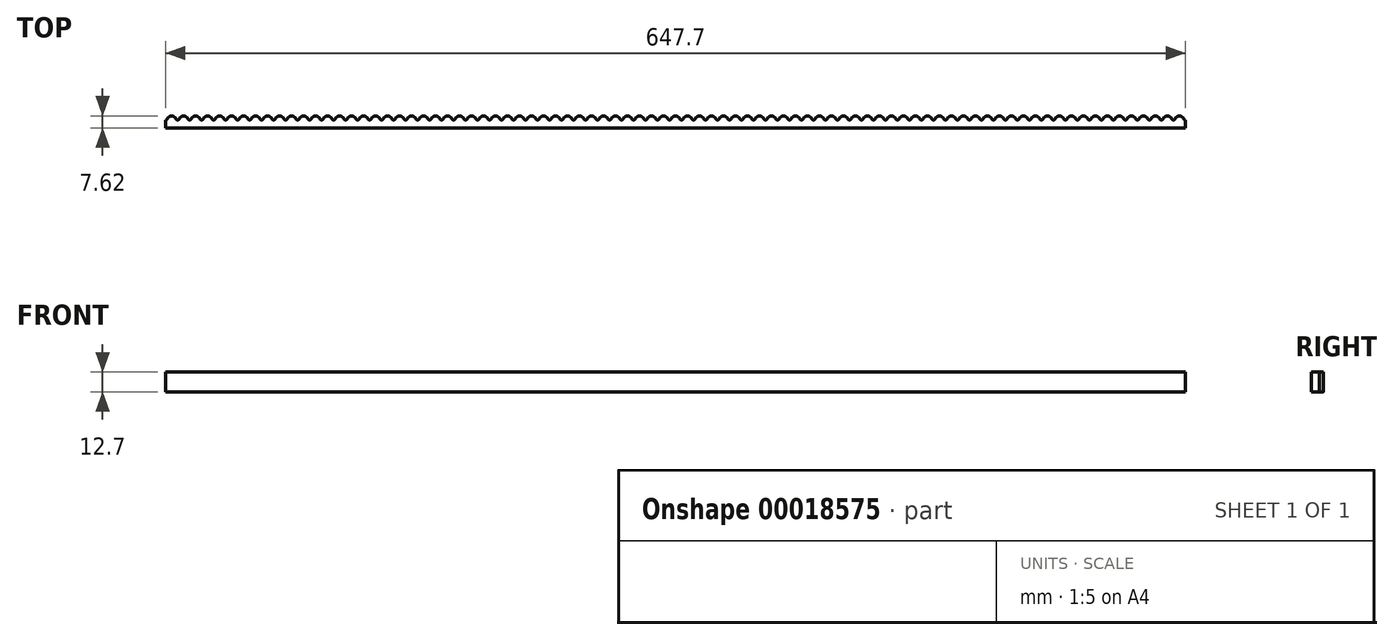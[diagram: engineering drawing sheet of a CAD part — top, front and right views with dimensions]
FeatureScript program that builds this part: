
annotation { "Feature Type Name" : "Feature", "Feature Type Description" : "" }
export const myFeature = defineFeature(function(context is Context, id is Id, definition is map)
    precondition{}
    {
        {
            var Q0;
            Q0=qCreatedBy(makeId("Top.planeOp"),FACE);
            var sketch = newSketch(context, id + "F0", { "sketchPlane" : qUnion([Q0])});
            skLineSegment(sketch, "E0.bottom", {"start": v(0, 0) * mm, "end": v(7.62, 0) * mm});
            skLineSegment(sketch, "E0.top", {"start": v(0, 7.62) * mm, "end": v(7.62, 7.62) * mm, "construction": true});
            skLineSegment(sketch, "E0.left", {"start": v(0, 0) * mm, "end": v(0, 7.62) * mm, "construction": true});
            skLineSegment(sketch, "E0.right", {"start": v(7.62, 0) * mm, "end": v(7.62, 7.62) * mm, "construction": true});
            skLineSegment(sketch, "E1", {"start": v(0, 5.08) * mm, "end": v(7.62, 5.08) * mm, "construction": true});
            skArc(sketch, "E2", {"start": v(0, 5.08) * mm, "mid": v(0.55, 5.21) * mm, "end": v(0.98, 5.58) * mm});
            skArc(sketch, "E3", {"start": v(5.98, 6.5) * mm, "mid": v(3.81, 7.62) * mm, "end": v(1.64, 6.5) * mm});
            skArc(sketch, "E4", {"start": v(6.64, 5.58) * mm, "mid": v(7.07, 5.21) * mm, "end": v(7.62, 5.08) * mm});
            skLineSegment(sketch, "E5", {"start": v(3.8, 5.08) * mm, "end": v(3.8, 7.62) * mm, "construction": true});
            skLineSegment(sketch, "E6", {"start": v(0.98, 5.58) * mm, "end": v(1.64, 6.5) * mm});
            skLineSegment(sketch, "E7", {"start": v(5.98, 6.5) * mm, "end": v(6.64, 5.58) * mm});
            skPoint(sketch, "E8.orphan", {"position": v(1.2, 6.28) * mm});
            skPoint(sketch, "E9.orphan", {"position": v(1.5, 6.28) * mm});
            skPoint(sketch, "E10.orphan", {"position": v(6.12, 6.28) * mm});
            skPoint(sketch, "E11.orphan", {"position": v(6.42, 6.28) * mm});
            skLineSegment(sketch, "E12.1.0.0", {"start": v(7.62, 0) * mm, "end": v(15.24, 0) * mm});
            skArc(sketch, "E12.1.0.1", {"start": v(13.6, 6.5) * mm, "mid": v(11.43, 7.62) * mm, "end": v(9.26, 6.5) * mm});
            skLineSegment(sketch, "E12.1.0.2", {"start": v(13.6, 6.5) * mm, "end": v(14.26, 5.58) * mm});
            skArc(sketch, "E12.1.0.3", {"start": v(7.62, 5.08) * mm, "mid": v(8.17, 5.21) * mm, "end": v(8.6, 5.58) * mm});
            skPoint(sketch, "E12.1.0.4", {"position": v(14.04, 6.28) * mm});
            skLineSegment(sketch, "E12.1.0.5", {"start": v(8.6, 5.58) * mm, "end": v(9.26, 6.5) * mm});
            skArc(sketch, "E12.1.0.6", {"start": v(14.26, 5.58) * mm, "mid": v(14.7, 5.21) * mm, "end": v(15.24, 5.08) * mm});
            skPoint(sketch, "E12.1.0.7", {"position": v(8.82, 6.28) * mm});
            skLineSegment(sketch, "E12.2.0.0", {"start": v(15.24, 0) * mm, "end": v(22.86, 0) * mm});
            skArc(sketch, "E12.2.0.1", {"start": v(21.22, 6.5) * mm, "mid": v(19.05, 7.62) * mm, "end": v(16.88, 6.5) * mm});
            skLineSegment(sketch, "E12.2.0.2", {"start": v(21.22, 6.5) * mm, "end": v(21.88, 5.58) * mm});
            skArc(sketch, "E12.2.0.3", {"start": v(15.24, 5.08) * mm, "mid": v(15.79, 5.21) * mm, "end": v(16.22, 5.58) * mm});
            skPoint(sketch, "E12.2.0.4", {"position": v(21.66, 6.28) * mm});
            skLineSegment(sketch, "E12.2.0.5", {"start": v(16.22, 5.58) * mm, "end": v(16.88, 6.5) * mm});
            skArc(sketch, "E12.2.0.6", {"start": v(21.88, 5.58) * mm, "mid": v(22.31, 5.21) * mm, "end": v(22.86, 5.08) * mm});
            skPoint(sketch, "E12.2.0.7", {"position": v(16.44, 6.28) * mm});
            skLineSegment(sketch, "E12.3.0.0", {"start": v(22.86, 0) * mm, "end": v(30.48, 0) * mm});
            skArc(sketch, "E12.3.0.1", {"start": v(28.84, 6.5) * mm, "mid": v(26.67, 7.62) * mm, "end": v(24.5, 6.5) * mm});
            skLineSegment(sketch, "E12.3.0.2", {"start": v(28.84, 6.5) * mm, "end": v(29.5, 5.58) * mm});
            skArc(sketch, "E12.3.0.3", {"start": v(22.86, 5.08) * mm, "mid": v(23.4, 5.21) * mm, "end": v(23.84, 5.58) * mm});
            skPoint(sketch, "E12.3.0.4", {"position": v(29.28, 6.28) * mm});
            skLineSegment(sketch, "E12.3.0.5", {"start": v(23.84, 5.58) * mm, "end": v(24.5, 6.5) * mm});
            skArc(sketch, "E12.3.0.6", {"start": v(29.5, 5.58) * mm, "mid": v(29.93, 5.21) * mm, "end": v(30.48, 5.08) * mm});
            skPoint(sketch, "E12.3.0.7", {"position": v(24.06, 6.28) * mm});
            skLineSegment(sketch, "E12.4.0.0", {"start": v(30.48, 0) * mm, "end": v(38.1, 0) * mm});
            skArc(sketch, "E12.4.0.1", {"start": v(36.46, 6.5) * mm, "mid": v(34.3, 7.62) * mm, "end": v(32.12, 6.5) * mm});
            skLineSegment(sketch, "E12.4.0.2", {"start": v(36.46, 6.5) * mm, "end": v(37.12, 5.58) * mm});
            skArc(sketch, "E12.4.0.3", {"start": v(30.48, 5.08) * mm, "mid": v(31.03, 5.21) * mm, "end": v(31.46, 5.58) * mm});
            skPoint(sketch, "E12.4.0.4", {"position": v(36.9, 6.28) * mm});
            skLineSegment(sketch, "E12.4.0.5", {"start": v(31.46, 5.58) * mm, "end": v(32.12, 6.5) * mm});
            skArc(sketch, "E12.4.0.6", {"start": v(37.12, 5.58) * mm, "mid": v(37.55, 5.21) * mm, "end": v(38.1, 5.08) * mm});
            skPoint(sketch, "E12.4.0.7", {"position": v(31.68, 6.28) * mm});
            skLineSegment(sketch, "E12.5.0.0", {"start": v(38.1, 0) * mm, "end": v(45.72, 0) * mm});
            skArc(sketch, "E12.5.0.1", {"start": v(44.08, 6.5) * mm, "mid": v(41.91, 7.62) * mm, "end": v(39.74, 6.5) * mm});
            skLineSegment(sketch, "E12.5.0.2", {"start": v(44.08, 6.5) * mm, "end": v(44.74, 5.58) * mm});
            skArc(sketch, "E12.5.0.3", {"start": v(38.1, 5.08) * mm, "mid": v(38.65, 5.21) * mm, "end": v(39.08, 5.58) * mm});
            skPoint(sketch, "E12.5.0.4", {"position": v(44.52, 6.28) * mm});
            skLineSegment(sketch, "E12.5.0.5", {"start": v(39.08, 5.58) * mm, "end": v(39.74, 6.5) * mm});
            skArc(sketch, "E12.5.0.6", {"start": v(44.74, 5.58) * mm, "mid": v(45.17, 5.21) * mm, "end": v(45.72, 5.08) * mm});
            skPoint(sketch, "E12.5.0.7", {"position": v(39.3, 6.28) * mm});
            skLineSegment(sketch, "E12.6.0.0", {"start": v(45.72, 0) * mm, "end": v(53.34, 0) * mm});
            skArc(sketch, "E12.6.0.1", {"start": v(51.7, 6.5) * mm, "mid": v(49.53, 7.62) * mm, "end": v(47.36, 6.5) * mm});
            skLineSegment(sketch, "E12.6.0.2", {"start": v(51.7, 6.5) * mm, "end": v(52.36, 5.58) * mm});
            skArc(sketch, "E12.6.0.3", {"start": v(45.72, 5.08) * mm, "mid": v(46.27, 5.21) * mm, "end": v(46.7, 5.58) * mm});
            skPoint(sketch, "E12.6.0.4", {"position": v(52.14, 6.28) * mm});
            skLineSegment(sketch, "E12.6.0.5", {"start": v(46.7, 5.58) * mm, "end": v(47.36, 6.5) * mm});
            skArc(sketch, "E12.6.0.6", {"start": v(52.36, 5.58) * mm, "mid": v(52.8, 5.21) * mm, "end": v(53.34, 5.08) * mm});
            skPoint(sketch, "E12.6.0.7", {"position": v(46.92, 6.28) * mm});
            skLineSegment(sketch, "E12.7.0.0", {"start": v(53.34, 0) * mm, "end": v(60.96, 0) * mm});
            skArc(sketch, "E12.7.0.1", {"start": v(59.32, 6.5) * mm, "mid": v(57.15, 7.62) * mm, "end": v(54.98, 6.5) * mm});
            skLineSegment(sketch, "E12.7.0.2", {"start": v(59.32, 6.5) * mm, "end": v(59.98, 5.58) * mm});
            skArc(sketch, "E12.7.0.3", {"start": v(53.34, 5.08) * mm, "mid": v(53.89, 5.21) * mm, "end": v(54.32, 5.58) * mm});
            skPoint(sketch, "E12.7.0.4", {"position": v(59.76, 6.28) * mm});
            skLineSegment(sketch, "E12.7.0.5", {"start": v(54.32, 5.58) * mm, "end": v(54.98, 6.5) * mm});
            skArc(sketch, "E12.7.0.6", {"start": v(59.98, 5.58) * mm, "mid": v(60.41, 5.21) * mm, "end": v(60.96, 5.08) * mm});
            skPoint(sketch, "E12.7.0.7", {"position": v(54.54, 6.28) * mm});
            skLineSegment(sketch, "E12.8.0.0", {"start": v(60.96, 0) * mm, "end": v(68.58, 0) * mm});
            skArc(sketch, "E12.8.0.1", {"start": v(66.94, 6.5) * mm, "mid": v(64.77, 7.62) * mm, "end": v(62.6, 6.5) * mm});
            skLineSegment(sketch, "E12.8.0.2", {"start": v(66.94, 6.5) * mm, "end": v(67.6, 5.58) * mm});
            skArc(sketch, "E12.8.0.3", {"start": v(60.96, 5.08) * mm, "mid": v(61.5, 5.21) * mm, "end": v(61.94, 5.58) * mm});
            skPoint(sketch, "E12.8.0.4", {"position": v(67.38, 6.28) * mm});
            skLineSegment(sketch, "E12.8.0.5", {"start": v(61.94, 5.58) * mm, "end": v(62.6, 6.5) * mm});
            skArc(sketch, "E12.8.0.6", {"start": v(67.6, 5.58) * mm, "mid": v(68.03, 5.21) * mm, "end": v(68.58, 5.08) * mm});
            skPoint(sketch, "E12.8.0.7", {"position": v(62.16, 6.28) * mm});
            skLineSegment(sketch, "E12.9.0.0", {"start": v(68.58, 0) * mm, "end": v(76.2, 0) * mm});
            skArc(sketch, "E12.9.0.1", {"start": v(74.56, 6.5) * mm, "mid": v(72.4, 7.62) * mm, "end": v(70.22, 6.5) * mm});
            skLineSegment(sketch, "E12.9.0.2", {"start": v(74.56, 6.5) * mm, "end": v(75.22, 5.58) * mm});
            skArc(sketch, "E12.9.0.3", {"start": v(68.58, 5.08) * mm, "mid": v(69.13, 5.21) * mm, "end": v(69.56, 5.58) * mm});
            skPoint(sketch, "E12.9.0.4", {"position": v(75, 6.28) * mm});
            skLineSegment(sketch, "E12.9.0.5", {"start": v(69.56, 5.58) * mm, "end": v(70.22, 6.5) * mm});
            skArc(sketch, "E12.9.0.6", {"start": v(75.22, 5.58) * mm, "mid": v(75.65, 5.21) * mm, "end": v(76.2, 5.08) * mm});
            skPoint(sketch, "E12.9.0.7", {"position": v(69.78, 6.28) * mm});
            skLineSegment(sketch, "E12.10.0.0", {"start": v(76.2, 0) * mm, "end": v(83.82, 0) * mm});
            skArc(sketch, "E12.10.0.1", {"start": v(82.18, 6.5) * mm, "mid": v(80.01, 7.62) * mm, "end": v(77.84, 6.5) * mm});
            skLineSegment(sketch, "E12.10.0.2", {"start": v(82.18, 6.5) * mm, "end": v(82.84, 5.58) * mm});
            skArc(sketch, "E12.10.0.3", {"start": v(76.2, 5.08) * mm, "mid": v(76.75, 5.21) * mm, "end": v(77.18, 5.58) * mm});
            skPoint(sketch, "E12.10.0.4", {"position": v(82.62, 6.28) * mm});
            skLineSegment(sketch, "E12.10.0.5", {"start": v(77.18, 5.58) * mm, "end": v(77.84, 6.5) * mm});
            skArc(sketch, "E12.10.0.6", {"start": v(82.84, 5.58) * mm, "mid": v(83.27, 5.21) * mm, "end": v(83.82, 5.08) * mm});
            skPoint(sketch, "E12.10.0.7", {"position": v(77.4, 6.28) * mm});
            skLineSegment(sketch, "E12.11.0.0", {"start": v(83.82, 0) * mm, "end": v(91.44, 0) * mm});
            skArc(sketch, "E12.11.0.1", {"start": v(89.8, 6.5) * mm, "mid": v(87.63, 7.62) * mm, "end": v(85.46, 6.5) * mm});
            skLineSegment(sketch, "E12.11.0.2", {"start": v(89.8, 6.5) * mm, "end": v(90.46, 5.58) * mm});
            skArc(sketch, "E12.11.0.3", {"start": v(83.82, 5.08) * mm, "mid": v(84.37, 5.21) * mm, "end": v(84.8, 5.58) * mm});
            skPoint(sketch, "E12.11.0.4", {"position": v(90.24, 6.28) * mm});
            skLineSegment(sketch, "E12.11.0.5", {"start": v(84.8, 5.58) * mm, "end": v(85.46, 6.5) * mm});
            skArc(sketch, "E12.11.0.6", {"start": v(90.46, 5.58) * mm, "mid": v(90.9, 5.21) * mm, "end": v(91.44, 5.08) * mm});
            skPoint(sketch, "E12.11.0.7", {"position": v(85.02, 6.28) * mm});
            skLineSegment(sketch, "E12.12.0.0", {"start": v(91.44, 0) * mm, "end": v(99.06, 0) * mm});
            skArc(sketch, "E12.12.0.1", {"start": v(97.42, 6.5) * mm, "mid": v(95.25, 7.62) * mm, "end": v(93.08, 6.5) * mm});
            skLineSegment(sketch, "E12.12.0.2", {"start": v(97.42, 6.5) * mm, "end": v(98.08, 5.58) * mm});
            skArc(sketch, "E12.12.0.3", {"start": v(91.44, 5.08) * mm, "mid": v(91.99, 5.21) * mm, "end": v(92.42, 5.58) * mm});
            skPoint(sketch, "E12.12.0.4", {"position": v(97.86, 6.28) * mm});
            skLineSegment(sketch, "E12.12.0.5", {"start": v(92.42, 5.58) * mm, "end": v(93.08, 6.5) * mm});
            skArc(sketch, "E12.12.0.6", {"start": v(98.08, 5.58) * mm, "mid": v(98.51, 5.21) * mm, "end": v(99.06, 5.08) * mm});
            skPoint(sketch, "E12.12.0.7", {"position": v(92.64, 6.28) * mm});
            skLineSegment(sketch, "E12.13.0.0", {"start": v(99.06, 0) * mm, "end": v(106.68, 0) * mm});
            skArc(sketch, "E12.13.0.1", {"start": v(105.04, 6.5) * mm, "mid": v(102.87, 7.62) * mm, "end": v(100.7, 6.5) * mm});
            skLineSegment(sketch, "E12.13.0.2", {"start": v(105.04, 6.5) * mm, "end": v(105.7, 5.58) * mm});
            skArc(sketch, "E12.13.0.3", {"start": v(99.06, 5.08) * mm, "mid": v(99.6, 5.21) * mm, "end": v(100.04, 5.58) * mm});
            skPoint(sketch, "E12.13.0.4", {"position": v(105.48, 6.28) * mm});
            skLineSegment(sketch, "E12.13.0.5", {"start": v(100.04, 5.58) * mm, "end": v(100.7, 6.5) * mm});
            skArc(sketch, "E12.13.0.6", {"start": v(105.7, 5.58) * mm, "mid": v(106.13, 5.21) * mm, "end": v(106.68, 5.08) * mm});
            skPoint(sketch, "E12.13.0.7", {"position": v(100.26, 6.28) * mm});
            skLineSegment(sketch, "E12.14.0.0", {"start": v(106.68, 0) * mm, "end": v(114.3, 0) * mm});
            skArc(sketch, "E12.14.0.1", {"start": v(112.66, 6.5) * mm, "mid": v(110.5, 7.62) * mm, "end": v(108.32, 6.5) * mm});
            skLineSegment(sketch, "E12.14.0.2", {"start": v(112.66, 6.5) * mm, "end": v(113.32, 5.58) * mm});
            skArc(sketch, "E12.14.0.3", {"start": v(106.68, 5.08) * mm, "mid": v(107.23, 5.21) * mm, "end": v(107.66, 5.58) * mm});
            skPoint(sketch, "E12.14.0.4", {"position": v(113.1, 6.28) * mm});
            skLineSegment(sketch, "E12.14.0.5", {"start": v(107.66, 5.58) * mm, "end": v(108.32, 6.5) * mm});
            skArc(sketch, "E12.14.0.6", {"start": v(113.32, 5.58) * mm, "mid": v(113.75, 5.21) * mm, "end": v(114.3, 5.08) * mm});
            skPoint(sketch, "E12.14.0.7", {"position": v(107.88, 6.28) * mm});
            skLineSegment(sketch, "E12.15.0.0", {"start": v(114.3, 0) * mm, "end": v(121.92, 0) * mm});
            skArc(sketch, "E12.15.0.1", {"start": v(120.28, 6.5) * mm, "mid": v(118.11, 7.62) * mm, "end": v(115.94, 6.5) * mm});
            skLineSegment(sketch, "E12.15.0.2", {"start": v(120.28, 6.5) * mm, "end": v(120.94, 5.58) * mm});
            skArc(sketch, "E12.15.0.3", {"start": v(114.3, 5.08) * mm, "mid": v(114.85, 5.21) * mm, "end": v(115.28, 5.58) * mm});
            skPoint(sketch, "E12.15.0.4", {"position": v(120.72, 6.28) * mm});
            skLineSegment(sketch, "E12.15.0.5", {"start": v(115.28, 5.58) * mm, "end": v(115.94, 6.5) * mm});
            skArc(sketch, "E12.15.0.6", {"start": v(120.94, 5.58) * mm, "mid": v(121.37, 5.21) * mm, "end": v(121.92, 5.08) * mm});
            skPoint(sketch, "E12.15.0.7", {"position": v(115.5, 6.28) * mm});
            skLineSegment(sketch, "E12.16.0.0", {"start": v(121.92, 0) * mm, "end": v(129.54, 0) * mm});
            skArc(sketch, "E12.16.0.1", {"start": v(127.9, 6.5) * mm, "mid": v(125.73, 7.62) * mm, "end": v(123.56, 6.5) * mm});
            skLineSegment(sketch, "E12.16.0.2", {"start": v(127.9, 6.5) * mm, "end": v(128.56, 5.58) * mm});
            skArc(sketch, "E12.16.0.3", {"start": v(121.92, 5.08) * mm, "mid": v(122.47, 5.21) * mm, "end": v(122.9, 5.58) * mm});
            skPoint(sketch, "E12.16.0.4", {"position": v(128.34, 6.28) * mm});
            skLineSegment(sketch, "E12.16.0.5", {"start": v(122.9, 5.58) * mm, "end": v(123.56, 6.5) * mm});
            skArc(sketch, "E12.16.0.6", {"start": v(128.56, 5.58) * mm, "mid": v(129, 5.21) * mm, "end": v(129.54, 5.08) * mm});
            skPoint(sketch, "E12.16.0.7", {"position": v(123.12, 6.28) * mm});
            skLineSegment(sketch, "E12.17.0.0", {"start": v(129.54, 0) * mm, "end": v(137.16, 0) * mm});
            skArc(sketch, "E12.17.0.1", {"start": v(135.52, 6.5) * mm, "mid": v(133.35, 7.62) * mm, "end": v(131.18, 6.5) * mm});
            skLineSegment(sketch, "E12.17.0.2", {"start": v(135.52, 6.5) * mm, "end": v(136.18, 5.58) * mm});
            skArc(sketch, "E12.17.0.3", {"start": v(129.54, 5.08) * mm, "mid": v(130.09, 5.21) * mm, "end": v(130.52, 5.58) * mm});
            skPoint(sketch, "E12.17.0.4", {"position": v(135.96, 6.28) * mm});
            skLineSegment(sketch, "E12.17.0.5", {"start": v(130.52, 5.58) * mm, "end": v(131.18, 6.5) * mm});
            skArc(sketch, "E12.17.0.6", {"start": v(136.18, 5.58) * mm, "mid": v(136.61, 5.21) * mm, "end": v(137.16, 5.08) * mm});
            skPoint(sketch, "E12.17.0.7", {"position": v(130.74, 6.28) * mm});
            skLineSegment(sketch, "E12.18.0.0", {"start": v(137.16, 0) * mm, "end": v(144.78, 0) * mm});
            skArc(sketch, "E12.18.0.1", {"start": v(143.14, 6.5) * mm, "mid": v(140.97, 7.62) * mm, "end": v(138.8, 6.5) * mm});
            skLineSegment(sketch, "E12.18.0.2", {"start": v(143.14, 6.5) * mm, "end": v(143.8, 5.58) * mm});
            skArc(sketch, "E12.18.0.3", {"start": v(137.16, 5.08) * mm, "mid": v(137.7, 5.21) * mm, "end": v(138.14, 5.58) * mm});
            skPoint(sketch, "E12.18.0.4", {"position": v(143.58, 6.28) * mm});
            skLineSegment(sketch, "E12.18.0.5", {"start": v(138.14, 5.58) * mm, "end": v(138.8, 6.5) * mm});
            skArc(sketch, "E12.18.0.6", {"start": v(143.8, 5.58) * mm, "mid": v(144.23, 5.21) * mm, "end": v(144.78, 5.08) * mm});
            skPoint(sketch, "E12.18.0.7", {"position": v(138.36, 6.28) * mm});
            skLineSegment(sketch, "E12.19.0.0", {"start": v(144.78, 0) * mm, "end": v(152.4, 0) * mm});
            skArc(sketch, "E12.19.0.1", {"start": v(150.76, 6.5) * mm, "mid": v(148.6, 7.62) * mm, "end": v(146.42, 6.5) * mm});
            skLineSegment(sketch, "E12.19.0.2", {"start": v(150.76, 6.5) * mm, "end": v(151.42, 5.58) * mm});
            skArc(sketch, "E12.19.0.3", {"start": v(144.78, 5.08) * mm, "mid": v(145.33, 5.21) * mm, "end": v(145.76, 5.58) * mm});
            skPoint(sketch, "E12.19.0.4", {"position": v(151.2, 6.28) * mm});
            skLineSegment(sketch, "E12.19.0.5", {"start": v(145.76, 5.58) * mm, "end": v(146.42, 6.5) * mm});
            skArc(sketch, "E12.19.0.6", {"start": v(151.42, 5.58) * mm, "mid": v(151.85, 5.21) * mm, "end": v(152.4, 5.08) * mm});
            skPoint(sketch, "E12.19.0.7", {"position": v(145.98, 6.28) * mm});
            skLineSegment(sketch, "E12.direction1", {"start": v(0, 0) * mm, "end": v(7.62, 0) * mm, "construction": true});
            skLineSegment(sketch, "E13.0.20.0", {"start": v(152.4, 0) * mm, "end": v(160.02, 0) * mm});
            skArc(sketch, "E13.3.20.0", {"start": v(158.38, 6.5) * mm, "mid": v(156.21, 7.62) * mm, "end": v(154.04, 6.5) * mm});
            skLineSegment(sketch, "E13.7.20.0", {"start": v(158.38, 6.5) * mm, "end": v(159.04, 5.58) * mm});
            skArc(sketch, "E13.10.20.0", {"start": v(152.4, 5.08) * mm, "mid": v(152.95, 5.21) * mm, "end": v(153.38, 5.58) * mm});
            skPoint(sketch, "E13.14.20.0", {"position": v(158.82, 6.28) * mm});
            skLineSegment(sketch, "E13.15.20.0", {"start": v(153.38, 5.58) * mm, "end": v(154.04, 6.5) * mm});
            skArc(sketch, "E13.18.20.0", {"start": v(159.04, 5.58) * mm, "mid": v(159.47, 5.21) * mm, "end": v(160.02, 5.08) * mm});
            skPoint(sketch, "E13.22.20.0", {"position": v(153.6, 6.28) * mm});
            skLineSegment(sketch, "E13.0.21.0", {"start": v(160.02, 0) * mm, "end": v(167.64, 0) * mm});
            skArc(sketch, "E13.3.21.0", {"start": v(166, 6.5) * mm, "mid": v(163.83, 7.62) * mm, "end": v(161.66, 6.5) * mm});
            skLineSegment(sketch, "E13.7.21.0", {"start": v(166, 6.5) * mm, "end": v(166.66, 5.58) * mm});
            skArc(sketch, "E13.10.21.0", {"start": v(160.02, 5.08) * mm, "mid": v(160.57, 5.21) * mm, "end": v(161, 5.58) * mm});
            skPoint(sketch, "E13.14.21.0", {"position": v(166.44, 6.28) * mm});
            skLineSegment(sketch, "E13.15.21.0", {"start": v(161, 5.58) * mm, "end": v(161.66, 6.5) * mm});
            skArc(sketch, "E13.18.21.0", {"start": v(166.66, 5.58) * mm, "mid": v(167.1, 5.21) * mm, "end": v(167.64, 5.08) * mm});
            skPoint(sketch, "E13.22.21.0", {"position": v(161.22, 6.28) * mm});
            skLineSegment(sketch, "E13.0.22.0", {"start": v(167.64, 0) * mm, "end": v(175.26, 0) * mm});
            skArc(sketch, "E13.3.22.0", {"start": v(173.62, 6.5) * mm, "mid": v(171.45, 7.62) * mm, "end": v(169.28, 6.5) * mm});
            skLineSegment(sketch, "E13.7.22.0", {"start": v(173.62, 6.5) * mm, "end": v(174.28, 5.58) * mm});
            skArc(sketch, "E13.10.22.0", {"start": v(167.64, 5.08) * mm, "mid": v(168.19, 5.21) * mm, "end": v(168.62, 5.58) * mm});
            skPoint(sketch, "E13.14.22.0", {"position": v(174.06, 6.28) * mm});
            skLineSegment(sketch, "E13.15.22.0", {"start": v(168.62, 5.58) * mm, "end": v(169.28, 6.5) * mm});
            skArc(sketch, "E13.18.22.0", {"start": v(174.28, 5.58) * mm, "mid": v(174.71, 5.21) * mm, "end": v(175.26, 5.08) * mm});
            skPoint(sketch, "E13.22.22.0", {"position": v(168.84, 6.28) * mm});
            skLineSegment(sketch, "E13.0.23.0", {"start": v(175.26, 0) * mm, "end": v(182.88, 0) * mm});
            skArc(sketch, "E13.3.23.0", {"start": v(181.24, 6.5) * mm, "mid": v(179.07, 7.62) * mm, "end": v(176.9, 6.5) * mm});
            skLineSegment(sketch, "E13.7.23.0", {"start": v(181.24, 6.5) * mm, "end": v(181.9, 5.58) * mm});
            skArc(sketch, "E13.10.23.0", {"start": v(175.26, 5.08) * mm, "mid": v(175.8, 5.21) * mm, "end": v(176.24, 5.58) * mm});
            skPoint(sketch, "E13.14.23.0", {"position": v(181.68, 6.28) * mm});
            skLineSegment(sketch, "E13.15.23.0", {"start": v(176.24, 5.58) * mm, "end": v(176.9, 6.5) * mm});
            skArc(sketch, "E13.18.23.0", {"start": v(181.9, 5.58) * mm, "mid": v(182.33, 5.21) * mm, "end": v(182.88, 5.08) * mm});
            skPoint(sketch, "E13.22.23.0", {"position": v(176.46, 6.28) * mm});
            skLineSegment(sketch, "E13.0.24.0", {"start": v(182.88, 0) * mm, "end": v(190.5, 0) * mm});
            skArc(sketch, "E13.3.24.0", {"start": v(188.86, 6.5) * mm, "mid": v(186.7, 7.62) * mm, "end": v(184.52, 6.5) * mm});
            skLineSegment(sketch, "E13.7.24.0", {"start": v(188.86, 6.5) * mm, "end": v(189.52, 5.58) * mm});
            skArc(sketch, "E13.10.24.0", {"start": v(182.88, 5.08) * mm, "mid": v(183.43, 5.21) * mm, "end": v(183.86, 5.58) * mm});
            skPoint(sketch, "E13.14.24.0", {"position": v(189.3, 6.28) * mm});
            skLineSegment(sketch, "E13.15.24.0", {"start": v(183.86, 5.58) * mm, "end": v(184.52, 6.5) * mm});
            skArc(sketch, "E13.18.24.0", {"start": v(189.52, 5.58) * mm, "mid": v(189.95, 5.21) * mm, "end": v(190.5, 5.08) * mm});
            skPoint(sketch, "E13.22.24.0", {"position": v(184.08, 6.28) * mm});
            skLineSegment(sketch, "E13.0.25.0", {"start": v(190.5, 0) * mm, "end": v(198.12, 0) * mm});
            skArc(sketch, "E13.3.25.0", {"start": v(196.48, 6.5) * mm, "mid": v(194.3, 7.62) * mm, "end": v(192.14, 6.5) * mm});
            skLineSegment(sketch, "E13.7.25.0", {"start": v(196.48, 6.5) * mm, "end": v(197.14, 5.58) * mm});
            skArc(sketch, "E13.10.25.0", {"start": v(190.5, 5.08) * mm, "mid": v(191.05, 5.21) * mm, "end": v(191.48, 5.58) * mm});
            skPoint(sketch, "E13.14.25.0", {"position": v(196.92, 6.28) * mm});
            skLineSegment(sketch, "E13.15.25.0", {"start": v(191.48, 5.58) * mm, "end": v(192.14, 6.5) * mm});
            skArc(sketch, "E13.18.25.0", {"start": v(197.14, 5.58) * mm, "mid": v(197.57, 5.21) * mm, "end": v(198.12, 5.08) * mm});
            skPoint(sketch, "E13.22.25.0", {"position": v(191.7, 6.28) * mm});
            skLineSegment(sketch, "E13.0.26.0", {"start": v(198.12, 0) * mm, "end": v(205.74, 0) * mm});
            skArc(sketch, "E13.3.26.0", {"start": v(204.1, 6.5) * mm, "mid": v(201.93, 7.62) * mm, "end": v(199.76, 6.5) * mm});
            skLineSegment(sketch, "E13.7.26.0", {"start": v(204.1, 6.5) * mm, "end": v(204.76, 5.58) * mm});
            skArc(sketch, "E13.10.26.0", {"start": v(198.12, 5.08) * mm, "mid": v(198.67, 5.21) * mm, "end": v(199.1, 5.58) * mm});
            skPoint(sketch, "E13.14.26.0", {"position": v(204.54, 6.28) * mm});
            skLineSegment(sketch, "E13.15.26.0", {"start": v(199.1, 5.58) * mm, "end": v(199.76, 6.5) * mm});
            skArc(sketch, "E13.18.26.0", {"start": v(204.76, 5.58) * mm, "mid": v(205.2, 5.21) * mm, "end": v(205.74, 5.08) * mm});
            skPoint(sketch, "E13.22.26.0", {"position": v(199.32, 6.28) * mm});
            skLineSegment(sketch, "E13.0.27.0", {"start": v(205.74, 0) * mm, "end": v(213.36, 0) * mm});
            skArc(sketch, "E13.3.27.0", {"start": v(211.72, 6.5) * mm, "mid": v(209.55, 7.62) * mm, "end": v(207.38, 6.5) * mm});
            skLineSegment(sketch, "E13.7.27.0", {"start": v(211.72, 6.5) * mm, "end": v(212.38, 5.58) * mm});
            skArc(sketch, "E13.10.27.0", {"start": v(205.74, 5.08) * mm, "mid": v(206.29, 5.21) * mm, "end": v(206.72, 5.58) * mm});
            skPoint(sketch, "E13.14.27.0", {"position": v(212.16, 6.28) * mm});
            skLineSegment(sketch, "E13.15.27.0", {"start": v(206.72, 5.58) * mm, "end": v(207.38, 6.5) * mm});
            skArc(sketch, "E13.18.27.0", {"start": v(212.38, 5.58) * mm, "mid": v(212.81, 5.21) * mm, "end": v(213.36, 5.08) * mm});
            skPoint(sketch, "E13.22.27.0", {"position": v(206.94, 6.28) * mm});
            skLineSegment(sketch, "E13.0.28.0", {"start": v(213.36, 0) * mm, "end": v(220.98, 0) * mm});
            skArc(sketch, "E13.3.28.0", {"start": v(219.34, 6.5) * mm, "mid": v(217.17, 7.62) * mm, "end": v(215, 6.5) * mm});
            skLineSegment(sketch, "E13.7.28.0", {"start": v(219.34, 6.5) * mm, "end": v(220, 5.58) * mm});
            skArc(sketch, "E13.10.28.0", {"start": v(213.36, 5.08) * mm, "mid": v(213.9, 5.21) * mm, "end": v(214.34, 5.58) * mm});
            skPoint(sketch, "E13.14.28.0", {"position": v(219.78, 6.28) * mm});
            skLineSegment(sketch, "E13.15.28.0", {"start": v(214.34, 5.58) * mm, "end": v(215, 6.5) * mm});
            skArc(sketch, "E13.18.28.0", {"start": v(220, 5.58) * mm, "mid": v(220.43, 5.21) * mm, "end": v(220.98, 5.08) * mm});
            skPoint(sketch, "E13.22.28.0", {"position": v(214.56, 6.28) * mm});
            skLineSegment(sketch, "E13.0.29.0", {"start": v(220.98, 0) * mm, "end": v(228.6, 0) * mm});
            skArc(sketch, "E13.3.29.0", {"start": v(226.96, 6.5) * mm, "mid": v(224.8, 7.62) * mm, "end": v(222.62, 6.5) * mm});
            skLineSegment(sketch, "E13.7.29.0", {"start": v(226.96, 6.5) * mm, "end": v(227.62, 5.58) * mm});
            skArc(sketch, "E13.10.29.0", {"start": v(220.98, 5.08) * mm, "mid": v(221.53, 5.21) * mm, "end": v(221.96, 5.58) * mm});
            skPoint(sketch, "E13.14.29.0", {"position": v(227.4, 6.28) * mm});
            skLineSegment(sketch, "E13.15.29.0", {"start": v(221.96, 5.58) * mm, "end": v(222.62, 6.5) * mm});
            skArc(sketch, "E13.18.29.0", {"start": v(227.62, 5.58) * mm, "mid": v(228.05, 5.21) * mm, "end": v(228.6, 5.08) * mm});
            skPoint(sketch, "E13.22.29.0", {"position": v(222.18, 6.28) * mm});
            skLineSegment(sketch, "E13.0.30.0", {"start": v(228.6, 0) * mm, "end": v(236.22, 0) * mm});
            skArc(sketch, "E13.3.30.0", {"start": v(234.58, 6.5) * mm, "mid": v(232.4, 7.62) * mm, "end": v(230.24, 6.5) * mm});
            skLineSegment(sketch, "E13.7.30.0", {"start": v(234.58, 6.5) * mm, "end": v(235.24, 5.58) * mm});
            skArc(sketch, "E13.10.30.0", {"start": v(228.6, 5.08) * mm, "mid": v(229.15, 5.21) * mm, "end": v(229.58, 5.58) * mm});
            skPoint(sketch, "E13.14.30.0", {"position": v(235.02, 6.28) * mm});
            skLineSegment(sketch, "E13.15.30.0", {"start": v(229.58, 5.58) * mm, "end": v(230.24, 6.5) * mm});
            skArc(sketch, "E13.18.30.0", {"start": v(235.24, 5.58) * mm, "mid": v(235.67, 5.21) * mm, "end": v(236.22, 5.08) * mm});
            skPoint(sketch, "E13.22.30.0", {"position": v(229.8, 6.28) * mm});
            skLineSegment(sketch, "E13.0.31.0", {"start": v(236.22, 0) * mm, "end": v(243.84, 0) * mm});
            skArc(sketch, "E13.3.31.0", {"start": v(242.2, 6.5) * mm, "mid": v(240.03, 7.62) * mm, "end": v(237.86, 6.5) * mm});
            skLineSegment(sketch, "E13.7.31.0", {"start": v(242.2, 6.5) * mm, "end": v(242.86, 5.58) * mm});
            skArc(sketch, "E13.10.31.0", {"start": v(236.22, 5.08) * mm, "mid": v(236.77, 5.21) * mm, "end": v(237.2, 5.58) * mm});
            skPoint(sketch, "E13.14.31.0", {"position": v(242.64, 6.28) * mm});
            skLineSegment(sketch, "E13.15.31.0", {"start": v(237.2, 5.58) * mm, "end": v(237.86, 6.5) * mm});
            skArc(sketch, "E13.18.31.0", {"start": v(242.86, 5.58) * mm, "mid": v(243.3, 5.21) * mm, "end": v(243.84, 5.08) * mm});
            skPoint(sketch, "E13.22.31.0", {"position": v(237.42, 6.28) * mm});
            skLineSegment(sketch, "E13.0.32.0", {"start": v(243.84, 0) * mm, "end": v(251.46, 0) * mm});
            skArc(sketch, "E13.3.32.0", {"start": v(249.82, 6.5) * mm, "mid": v(247.65, 7.62) * mm, "end": v(245.48, 6.5) * mm});
            skLineSegment(sketch, "E13.7.32.0", {"start": v(249.82, 6.5) * mm, "end": v(250.48, 5.58) * mm});
            skArc(sketch, "E13.10.32.0", {"start": v(243.84, 5.08) * mm, "mid": v(244.39, 5.21) * mm, "end": v(244.82, 5.58) * mm});
            skPoint(sketch, "E13.14.32.0", {"position": v(250.26, 6.28) * mm});
            skLineSegment(sketch, "E13.15.32.0", {"start": v(244.82, 5.58) * mm, "end": v(245.48, 6.5) * mm});
            skArc(sketch, "E13.18.32.0", {"start": v(250.48, 5.58) * mm, "mid": v(250.91, 5.21) * mm, "end": v(251.46, 5.08) * mm});
            skPoint(sketch, "E13.22.32.0", {"position": v(245.04, 6.28) * mm});
            skLineSegment(sketch, "E13.0.33.0", {"start": v(251.46, 0) * mm, "end": v(259.08, 0) * mm});
            skArc(sketch, "E13.3.33.0", {"start": v(257.44, 6.5) * mm, "mid": v(255.27, 7.62) * mm, "end": v(253.1, 6.5) * mm});
            skLineSegment(sketch, "E13.7.33.0", {"start": v(257.44, 6.5) * mm, "end": v(258.1, 5.58) * mm});
            skArc(sketch, "E13.10.33.0", {"start": v(251.46, 5.08) * mm, "mid": v(252, 5.21) * mm, "end": v(252.44, 5.58) * mm});
            skPoint(sketch, "E13.14.33.0", {"position": v(257.88, 6.28) * mm});
            skLineSegment(sketch, "E13.15.33.0", {"start": v(252.44, 5.58) * mm, "end": v(253.1, 6.5) * mm});
            skArc(sketch, "E13.18.33.0", {"start": v(258.1, 5.58) * mm, "mid": v(258.53, 5.21) * mm, "end": v(259.08, 5.08) * mm});
            skPoint(sketch, "E13.22.33.0", {"position": v(252.66, 6.28) * mm});
            skLineSegment(sketch, "E13.0.34.0", {"start": v(259.08, 0) * mm, "end": v(266.7, 0) * mm});
            skArc(sketch, "E13.3.34.0", {"start": v(265.06, 6.5) * mm, "mid": v(262.9, 7.62) * mm, "end": v(260.72, 6.5) * mm});
            skLineSegment(sketch, "E13.7.34.0", {"start": v(265.06, 6.5) * mm, "end": v(265.72, 5.58) * mm});
            skArc(sketch, "E13.10.34.0", {"start": v(259.08, 5.08) * mm, "mid": v(259.63, 5.21) * mm, "end": v(260.06, 5.58) * mm});
            skPoint(sketch, "E13.14.34.0", {"position": v(265.5, 6.28) * mm});
            skLineSegment(sketch, "E13.15.34.0", {"start": v(260.06, 5.58) * mm, "end": v(260.72, 6.5) * mm});
            skArc(sketch, "E13.18.34.0", {"start": v(265.72, 5.58) * mm, "mid": v(266.15, 5.21) * mm, "end": v(266.7, 5.08) * mm});
            skPoint(sketch, "E13.22.34.0", {"position": v(260.28, 6.28) * mm});
            skLineSegment(sketch, "E13.0.35.0", {"start": v(266.7, 0) * mm, "end": v(274.32, 0) * mm});
            skArc(sketch, "E13.3.35.0", {"start": v(272.68, 6.5) * mm, "mid": v(270.51, 7.62) * mm, "end": v(268.34, 6.5) * mm});
            skLineSegment(sketch, "E13.7.35.0", {"start": v(272.68, 6.5) * mm, "end": v(273.34, 5.58) * mm});
            skArc(sketch, "E13.10.35.0", {"start": v(266.7, 5.08) * mm, "mid": v(267.25, 5.21) * mm, "end": v(267.68, 5.58) * mm});
            skPoint(sketch, "E13.14.35.0", {"position": v(273.12, 6.28) * mm});
            skLineSegment(sketch, "E13.15.35.0", {"start": v(267.68, 5.58) * mm, "end": v(268.34, 6.5) * mm});
            skArc(sketch, "E13.18.35.0", {"start": v(273.34, 5.58) * mm, "mid": v(273.77, 5.21) * mm, "end": v(274.32, 5.08) * mm});
            skPoint(sketch, "E13.22.35.0", {"position": v(267.9, 6.28) * mm});
            skLineSegment(sketch, "E13.0.36.0", {"start": v(274.32, 0) * mm, "end": v(281.94, 0) * mm});
            skArc(sketch, "E13.3.36.0", {"start": v(280.3, 6.5) * mm, "mid": v(278.13, 7.62) * mm, "end": v(275.96, 6.5) * mm});
            skLineSegment(sketch, "E13.7.36.0", {"start": v(280.3, 6.5) * mm, "end": v(280.96, 5.58) * mm});
            skArc(sketch, "E13.10.36.0", {"start": v(274.32, 5.08) * mm, "mid": v(274.87, 5.21) * mm, "end": v(275.3, 5.58) * mm});
            skPoint(sketch, "E13.14.36.0", {"position": v(280.74, 6.28) * mm});
            skLineSegment(sketch, "E13.15.36.0", {"start": v(275.3, 5.58) * mm, "end": v(275.96, 6.5) * mm});
            skArc(sketch, "E13.18.36.0", {"start": v(280.96, 5.58) * mm, "mid": v(281.4, 5.21) * mm, "end": v(281.94, 5.08) * mm});
            skPoint(sketch, "E13.22.36.0", {"position": v(275.52, 6.28) * mm});
            skLineSegment(sketch, "E13.0.37.0", {"start": v(281.94, 0) * mm, "end": v(289.56, 0) * mm});
            skArc(sketch, "E13.3.37.0", {"start": v(287.92, 6.5) * mm, "mid": v(285.75, 7.62) * mm, "end": v(283.58, 6.5) * mm});
            skLineSegment(sketch, "E13.7.37.0", {"start": v(287.92, 6.5) * mm, "end": v(288.58, 5.58) * mm});
            skArc(sketch, "E13.10.37.0", {"start": v(281.94, 5.08) * mm, "mid": v(282.49, 5.21) * mm, "end": v(282.92, 5.58) * mm});
            skPoint(sketch, "E13.14.37.0", {"position": v(288.36, 6.28) * mm});
            skLineSegment(sketch, "E13.15.37.0", {"start": v(282.92, 5.58) * mm, "end": v(283.58, 6.5) * mm});
            skArc(sketch, "E13.18.37.0", {"start": v(288.58, 5.58) * mm, "mid": v(289.01, 5.21) * mm, "end": v(289.56, 5.08) * mm});
            skPoint(sketch, "E13.22.37.0", {"position": v(283.14, 6.28) * mm});
            skLineSegment(sketch, "E13.0.38.0", {"start": v(289.56, 0) * mm, "end": v(297.18, 0) * mm});
            skArc(sketch, "E13.3.38.0", {"start": v(295.54, 6.5) * mm, "mid": v(293.37, 7.62) * mm, "end": v(291.2, 6.5) * mm});
            skLineSegment(sketch, "E13.7.38.0", {"start": v(295.54, 6.5) * mm, "end": v(296.2, 5.58) * mm});
            skArc(sketch, "E13.10.38.0", {"start": v(289.56, 5.08) * mm, "mid": v(290.1, 5.21) * mm, "end": v(290.54, 5.58) * mm});
            skPoint(sketch, "E13.14.38.0", {"position": v(295.98, 6.28) * mm});
            skLineSegment(sketch, "E13.15.38.0", {"start": v(290.54, 5.58) * mm, "end": v(291.2, 6.5) * mm});
            skArc(sketch, "E13.18.38.0", {"start": v(296.2, 5.58) * mm, "mid": v(296.63, 5.21) * mm, "end": v(297.18, 5.08) * mm});
            skPoint(sketch, "E13.22.38.0", {"position": v(290.76, 6.28) * mm});
            skLineSegment(sketch, "E13.0.39.0", {"start": v(297.18, 0) * mm, "end": v(304.8, 0) * mm});
            skArc(sketch, "E13.3.39.0", {"start": v(303.16, 6.5) * mm, "mid": v(301, 7.62) * mm, "end": v(298.82, 6.5) * mm});
            skLineSegment(sketch, "E13.7.39.0", {"start": v(303.16, 6.5) * mm, "end": v(303.82, 5.58) * mm});
            skArc(sketch, "E13.10.39.0", {"start": v(297.18, 5.08) * mm, "mid": v(297.73, 5.21) * mm, "end": v(298.16, 5.58) * mm});
            skPoint(sketch, "E13.14.39.0", {"position": v(303.6, 6.28) * mm});
            skLineSegment(sketch, "E13.15.39.0", {"start": v(298.16, 5.58) * mm, "end": v(298.82, 6.5) * mm});
            skArc(sketch, "E13.18.39.0", {"start": v(303.82, 5.58) * mm, "mid": v(304.25, 5.21) * mm, "end": v(304.8, 5.08) * mm});
            skPoint(sketch, "E13.22.39.0", {"position": v(298.38, 6.28) * mm});
            skLineSegment(sketch, "E13.0.40.0", {"start": v(304.8, 0) * mm, "end": v(312.42, 0) * mm});
            skArc(sketch, "E13.3.40.0", {"start": v(310.78, 6.5) * mm, "mid": v(308.61, 7.62) * mm, "end": v(306.44, 6.5) * mm});
            skLineSegment(sketch, "E13.7.40.0", {"start": v(310.78, 6.5) * mm, "end": v(311.44, 5.58) * mm});
            skArc(sketch, "E13.10.40.0", {"start": v(304.8, 5.08) * mm, "mid": v(305.35, 5.21) * mm, "end": v(305.78, 5.58) * mm});
            skPoint(sketch, "E13.14.40.0", {"position": v(311.22, 6.28) * mm});
            skLineSegment(sketch, "E13.15.40.0", {"start": v(305.78, 5.58) * mm, "end": v(306.44, 6.5) * mm});
            skArc(sketch, "E13.18.40.0", {"start": v(311.44, 5.58) * mm, "mid": v(311.87, 5.21) * mm, "end": v(312.42, 5.08) * mm});
            skPoint(sketch, "E13.22.40.0", {"position": v(306, 6.28) * mm});
            skLineSegment(sketch, "E13.0.41.0", {"start": v(312.42, 0) * mm, "end": v(320.04, 0) * mm});
            skArc(sketch, "E13.3.41.0", {"start": v(318.4, 6.5) * mm, "mid": v(316.23, 7.62) * mm, "end": v(314.06, 6.5) * mm});
            skLineSegment(sketch, "E13.7.41.0", {"start": v(318.4, 6.5) * mm, "end": v(319.06, 5.58) * mm});
            skArc(sketch, "E13.10.41.0", {"start": v(312.42, 5.08) * mm, "mid": v(312.97, 5.21) * mm, "end": v(313.4, 5.58) * mm});
            skPoint(sketch, "E13.14.41.0", {"position": v(318.84, 6.28) * mm});
            skLineSegment(sketch, "E13.15.41.0", {"start": v(313.4, 5.58) * mm, "end": v(314.06, 6.5) * mm});
            skArc(sketch, "E13.18.41.0", {"start": v(319.06, 5.58) * mm, "mid": v(319.5, 5.21) * mm, "end": v(320.04, 5.08) * mm});
            skPoint(sketch, "E13.22.41.0", {"position": v(313.62, 6.28) * mm});
            skLineSegment(sketch, "E13.0.42.0", {"start": v(320.04, 0) * mm, "end": v(327.66, 0) * mm});
            skArc(sketch, "E13.3.42.0", {"start": v(326.02, 6.5) * mm, "mid": v(323.85, 7.62) * mm, "end": v(321.68, 6.5) * mm});
            skLineSegment(sketch, "E13.7.42.0", {"start": v(326.02, 6.5) * mm, "end": v(326.68, 5.58) * mm});
            skArc(sketch, "E13.10.42.0", {"start": v(320.04, 5.08) * mm, "mid": v(320.59, 5.21) * mm, "end": v(321.02, 5.58) * mm});
            skPoint(sketch, "E13.14.42.0", {"position": v(326.46, 6.28) * mm});
            skLineSegment(sketch, "E13.15.42.0", {"start": v(321.02, 5.58) * mm, "end": v(321.68, 6.5) * mm});
            skArc(sketch, "E13.18.42.0", {"start": v(326.68, 5.58) * mm, "mid": v(327.11, 5.21) * mm, "end": v(327.66, 5.08) * mm});
            skPoint(sketch, "E13.22.42.0", {"position": v(321.24, 6.28) * mm});
            skLineSegment(sketch, "E13.0.43.0", {"start": v(327.66, 0) * mm, "end": v(335.28, 0) * mm});
            skArc(sketch, "E13.3.43.0", {"start": v(333.64, 6.5) * mm, "mid": v(331.47, 7.62) * mm, "end": v(329.3, 6.5) * mm});
            skLineSegment(sketch, "E13.7.43.0", {"start": v(333.64, 6.5) * mm, "end": v(334.3, 5.58) * mm});
            skArc(sketch, "E13.10.43.0", {"start": v(327.66, 5.08) * mm, "mid": v(328.2, 5.21) * mm, "end": v(328.64, 5.58) * mm});
            skPoint(sketch, "E13.14.43.0", {"position": v(334.08, 6.28) * mm});
            skLineSegment(sketch, "E13.15.43.0", {"start": v(328.64, 5.58) * mm, "end": v(329.3, 6.5) * mm});
            skArc(sketch, "E13.18.43.0", {"start": v(334.3, 5.58) * mm, "mid": v(334.73, 5.21) * mm, "end": v(335.28, 5.08) * mm});
            skPoint(sketch, "E13.22.43.0", {"position": v(328.86, 6.28) * mm});
            skLineSegment(sketch, "E13.0.44.0", {"start": v(335.28, 0) * mm, "end": v(342.9, 0) * mm});
            skArc(sketch, "E13.3.44.0", {"start": v(341.26, 6.5) * mm, "mid": v(339.1, 7.62) * mm, "end": v(336.92, 6.5) * mm});
            skLineSegment(sketch, "E13.7.44.0", {"start": v(341.26, 6.5) * mm, "end": v(341.92, 5.58) * mm});
            skArc(sketch, "E13.10.44.0", {"start": v(335.28, 5.08) * mm, "mid": v(335.83, 5.21) * mm, "end": v(336.26, 5.58) * mm});
            skPoint(sketch, "E13.14.44.0", {"position": v(341.7, 6.28) * mm});
            skLineSegment(sketch, "E13.15.44.0", {"start": v(336.26, 5.58) * mm, "end": v(336.92, 6.5) * mm});
            skArc(sketch, "E13.18.44.0", {"start": v(341.92, 5.58) * mm, "mid": v(342.35, 5.21) * mm, "end": v(342.9, 5.08) * mm});
            skPoint(sketch, "E13.22.44.0", {"position": v(336.48, 6.28) * mm});
            skLineSegment(sketch, "E13.0.45.0", {"start": v(342.9, 0) * mm, "end": v(350.52, 0) * mm});
            skArc(sketch, "E13.3.45.0", {"start": v(348.88, 6.5) * mm, "mid": v(346.71, 7.62) * mm, "end": v(344.54, 6.5) * mm});
            skLineSegment(sketch, "E13.7.45.0", {"start": v(348.88, 6.5) * mm, "end": v(349.54, 5.58) * mm});
            skArc(sketch, "E13.10.45.0", {"start": v(342.9, 5.08) * mm, "mid": v(343.45, 5.21) * mm, "end": v(343.88, 5.58) * mm});
            skPoint(sketch, "E13.14.45.0", {"position": v(349.32, 6.28) * mm});
            skLineSegment(sketch, "E13.15.45.0", {"start": v(343.88, 5.58) * mm, "end": v(344.54, 6.5) * mm});
            skArc(sketch, "E13.18.45.0", {"start": v(349.54, 5.58) * mm, "mid": v(349.97, 5.21) * mm, "end": v(350.52, 5.08) * mm});
            skPoint(sketch, "E13.22.45.0", {"position": v(344.1, 6.28) * mm});
            skLineSegment(sketch, "E13.0.46.0", {"start": v(350.52, 0) * mm, "end": v(358.14, 0) * mm});
            skArc(sketch, "E13.3.46.0", {"start": v(356.5, 6.5) * mm, "mid": v(354.33, 7.62) * mm, "end": v(352.16, 6.5) * mm});
            skLineSegment(sketch, "E13.7.46.0", {"start": v(356.5, 6.5) * mm, "end": v(357.16, 5.58) * mm});
            skArc(sketch, "E13.10.46.0", {"start": v(350.52, 5.08) * mm, "mid": v(351.07, 5.21) * mm, "end": v(351.5, 5.58) * mm});
            skPoint(sketch, "E13.14.46.0", {"position": v(356.94, 6.28) * mm});
            skLineSegment(sketch, "E13.15.46.0", {"start": v(351.5, 5.58) * mm, "end": v(352.16, 6.5) * mm});
            skArc(sketch, "E13.18.46.0", {"start": v(357.16, 5.58) * mm, "mid": v(357.6, 5.21) * mm, "end": v(358.14, 5.08) * mm});
            skPoint(sketch, "E13.22.46.0", {"position": v(351.72, 6.28) * mm});
            skLineSegment(sketch, "E13.0.47.0", {"start": v(358.14, 0) * mm, "end": v(365.76, 0) * mm});
            skArc(sketch, "E13.3.47.0", {"start": v(364.12, 6.5) * mm, "mid": v(361.95, 7.62) * mm, "end": v(359.78, 6.5) * mm});
            skLineSegment(sketch, "E13.7.47.0", {"start": v(364.12, 6.5) * mm, "end": v(364.78, 5.58) * mm});
            skArc(sketch, "E13.10.47.0", {"start": v(358.14, 5.08) * mm, "mid": v(358.69, 5.21) * mm, "end": v(359.12, 5.58) * mm});
            skPoint(sketch, "E13.14.47.0", {"position": v(364.56, 6.28) * mm});
            skLineSegment(sketch, "E13.15.47.0", {"start": v(359.12, 5.58) * mm, "end": v(359.78, 6.5) * mm});
            skArc(sketch, "E13.18.47.0", {"start": v(364.78, 5.58) * mm, "mid": v(365.21, 5.21) * mm, "end": v(365.76, 5.08) * mm});
            skPoint(sketch, "E13.22.47.0", {"position": v(359.34, 6.28) * mm});
            skLineSegment(sketch, "E13.0.48.0", {"start": v(365.76, 0) * mm, "end": v(373.38, 0) * mm});
            skArc(sketch, "E13.3.48.0", {"start": v(371.74, 6.5) * mm, "mid": v(369.57, 7.62) * mm, "end": v(367.4, 6.5) * mm});
            skLineSegment(sketch, "E13.7.48.0", {"start": v(371.74, 6.5) * mm, "end": v(372.4, 5.58) * mm});
            skArc(sketch, "E13.10.48.0", {"start": v(365.76, 5.08) * mm, "mid": v(366.3, 5.21) * mm, "end": v(366.74, 5.58) * mm});
            skPoint(sketch, "E13.14.48.0", {"position": v(372.18, 6.28) * mm});
            skLineSegment(sketch, "E13.15.48.0", {"start": v(366.74, 5.58) * mm, "end": v(367.4, 6.5) * mm});
            skArc(sketch, "E13.18.48.0", {"start": v(372.4, 5.58) * mm, "mid": v(372.83, 5.21) * mm, "end": v(373.38, 5.08) * mm});
            skPoint(sketch, "E13.22.48.0", {"position": v(366.96, 6.28) * mm});
            skLineSegment(sketch, "E13.0.49.0", {"start": v(373.38, 0) * mm, "end": v(381, 0) * mm});
            skArc(sketch, "E13.3.49.0", {"start": v(379.36, 6.5) * mm, "mid": v(377.2, 7.62) * mm, "end": v(375.02, 6.5) * mm});
            skLineSegment(sketch, "E13.7.49.0", {"start": v(379.36, 6.5) * mm, "end": v(380.02, 5.58) * mm});
            skArc(sketch, "E13.10.49.0", {"start": v(373.38, 5.08) * mm, "mid": v(373.93, 5.21) * mm, "end": v(374.36, 5.58) * mm});
            skPoint(sketch, "E13.14.49.0", {"position": v(379.8, 6.28) * mm});
            skLineSegment(sketch, "E13.15.49.0", {"start": v(374.36, 5.58) * mm, "end": v(375.02, 6.5) * mm});
            skArc(sketch, "E13.18.49.0", {"start": v(380.02, 5.58) * mm, "mid": v(380.45, 5.21) * mm, "end": v(381, 5.08) * mm});
            skPoint(sketch, "E13.22.49.0", {"position": v(374.58, 6.28) * mm});
            skLineSegment(sketch, "E14.0.50.0", {"start": v(381, 0) * mm, "end": v(388.62, 0) * mm});
            skArc(sketch, "E14.3.50.0", {"start": v(386.98, 6.5) * mm, "mid": v(384.81, 7.62) * mm, "end": v(382.64, 6.5) * mm});
            skLineSegment(sketch, "E14.7.50.0", {"start": v(386.98, 6.5) * mm, "end": v(387.64, 5.58) * mm});
            skArc(sketch, "E14.10.50.0", {"start": v(381, 5.08) * mm, "mid": v(381.55, 5.21) * mm, "end": v(381.98, 5.58) * mm});
            skPoint(sketch, "E14.14.50.0", {"position": v(387.42, 6.28) * mm});
            skLineSegment(sketch, "E14.15.50.0", {"start": v(381.98, 5.58) * mm, "end": v(382.64, 6.5) * mm});
            skArc(sketch, "E14.18.50.0", {"start": v(387.64, 5.58) * mm, "mid": v(388.07, 5.21) * mm, "end": v(388.62, 5.08) * mm});
            skPoint(sketch, "E14.22.50.0", {"position": v(382.2, 6.28) * mm});
            skLineSegment(sketch, "E14.0.51.0", {"start": v(388.62, 0) * mm, "end": v(396.24, 0) * mm});
            skArc(sketch, "E14.3.51.0", {"start": v(394.6, 6.5) * mm, "mid": v(392.43, 7.62) * mm, "end": v(390.26, 6.5) * mm});
            skLineSegment(sketch, "E14.7.51.0", {"start": v(394.6, 6.5) * mm, "end": v(395.26, 5.58) * mm});
            skArc(sketch, "E14.10.51.0", {"start": v(388.62, 5.08) * mm, "mid": v(389.17, 5.21) * mm, "end": v(389.6, 5.58) * mm});
            skPoint(sketch, "E14.14.51.0", {"position": v(395.04, 6.28) * mm});
            skLineSegment(sketch, "E14.15.51.0", {"start": v(389.6, 5.58) * mm, "end": v(390.26, 6.5) * mm});
            skArc(sketch, "E14.18.51.0", {"start": v(395.26, 5.58) * mm, "mid": v(395.7, 5.21) * mm, "end": v(396.24, 5.08) * mm});
            skPoint(sketch, "E14.22.51.0", {"position": v(389.82, 6.28) * mm});
            skLineSegment(sketch, "E14.0.52.0", {"start": v(396.24, 0) * mm, "end": v(403.86, 0) * mm});
            skArc(sketch, "E14.3.52.0", {"start": v(402.22, 6.5) * mm, "mid": v(400.05, 7.62) * mm, "end": v(397.88, 6.5) * mm});
            skLineSegment(sketch, "E14.7.52.0", {"start": v(402.22, 6.5) * mm, "end": v(402.88, 5.58) * mm});
            skArc(sketch, "E14.10.52.0", {"start": v(396.24, 5.08) * mm, "mid": v(396.79, 5.21) * mm, "end": v(397.22, 5.58) * mm});
            skPoint(sketch, "E14.14.52.0", {"position": v(402.66, 6.28) * mm});
            skLineSegment(sketch, "E14.15.52.0", {"start": v(397.22, 5.58) * mm, "end": v(397.88, 6.5) * mm});
            skArc(sketch, "E14.18.52.0", {"start": v(402.88, 5.58) * mm, "mid": v(403.31, 5.21) * mm, "end": v(403.86, 5.08) * mm});
            skPoint(sketch, "E14.22.52.0", {"position": v(397.44, 6.28) * mm});
            skLineSegment(sketch, "E14.0.53.0", {"start": v(403.86, 0) * mm, "end": v(411.48, 0) * mm});
            skArc(sketch, "E14.3.53.0", {"start": v(409.84, 6.5) * mm, "mid": v(407.67, 7.62) * mm, "end": v(405.5, 6.5) * mm});
            skLineSegment(sketch, "E14.7.53.0", {"start": v(409.84, 6.5) * mm, "end": v(410.5, 5.58) * mm});
            skArc(sketch, "E14.10.53.0", {"start": v(403.86, 5.08) * mm, "mid": v(404.4, 5.21) * mm, "end": v(404.84, 5.58) * mm});
            skPoint(sketch, "E14.14.53.0", {"position": v(410.28, 6.28) * mm});
            skLineSegment(sketch, "E14.15.53.0", {"start": v(404.84, 5.58) * mm, "end": v(405.5, 6.5) * mm});
            skArc(sketch, "E14.18.53.0", {"start": v(410.5, 5.58) * mm, "mid": v(410.93, 5.21) * mm, "end": v(411.48, 5.08) * mm});
            skPoint(sketch, "E14.22.53.0", {"position": v(405.06, 6.28) * mm});
            skLineSegment(sketch, "E14.0.54.0", {"start": v(411.48, 0) * mm, "end": v(419.1, 0) * mm});
            skArc(sketch, "E14.3.54.0", {"start": v(417.46, 6.5) * mm, "mid": v(415.3, 7.62) * mm, "end": v(413.12, 6.5) * mm});
            skLineSegment(sketch, "E14.7.54.0", {"start": v(417.46, 6.5) * mm, "end": v(418.12, 5.58) * mm});
            skArc(sketch, "E14.10.54.0", {"start": v(411.48, 5.08) * mm, "mid": v(412.03, 5.21) * mm, "end": v(412.46, 5.58) * mm});
            skPoint(sketch, "E14.14.54.0", {"position": v(417.9, 6.28) * mm});
            skLineSegment(sketch, "E14.15.54.0", {"start": v(412.46, 5.58) * mm, "end": v(413.12, 6.5) * mm});
            skArc(sketch, "E14.18.54.0", {"start": v(418.12, 5.58) * mm, "mid": v(418.55, 5.21) * mm, "end": v(419.1, 5.08) * mm});
            skPoint(sketch, "E14.22.54.0", {"position": v(412.68, 6.28) * mm});
            skLineSegment(sketch, "E14.0.55.0", {"start": v(419.1, 0) * mm, "end": v(426.72, 0) * mm});
            skArc(sketch, "E14.3.55.0", {"start": v(425.08, 6.5) * mm, "mid": v(422.91, 7.62) * mm, "end": v(420.74, 6.5) * mm});
            skLineSegment(sketch, "E14.7.55.0", {"start": v(425.08, 6.5) * mm, "end": v(425.74, 5.58) * mm});
            skArc(sketch, "E14.10.55.0", {"start": v(419.1, 5.08) * mm, "mid": v(419.65, 5.21) * mm, "end": v(420.08, 5.58) * mm});
            skPoint(sketch, "E14.14.55.0", {"position": v(425.52, 6.28) * mm});
            skLineSegment(sketch, "E14.15.55.0", {"start": v(420.08, 5.58) * mm, "end": v(420.74, 6.5) * mm});
            skArc(sketch, "E14.18.55.0", {"start": v(425.74, 5.58) * mm, "mid": v(426.17, 5.21) * mm, "end": v(426.72, 5.08) * mm});
            skPoint(sketch, "E14.22.55.0", {"position": v(420.3, 6.28) * mm});
            skLineSegment(sketch, "E14.0.56.0", {"start": v(426.72, 0) * mm, "end": v(434.34, 0) * mm});
            skArc(sketch, "E14.3.56.0", {"start": v(432.7, 6.5) * mm, "mid": v(430.53, 7.62) * mm, "end": v(428.36, 6.5) * mm});
            skLineSegment(sketch, "E14.7.56.0", {"start": v(432.7, 6.5) * mm, "end": v(433.36, 5.58) * mm});
            skArc(sketch, "E14.10.56.0", {"start": v(426.72, 5.08) * mm, "mid": v(427.27, 5.21) * mm, "end": v(427.7, 5.58) * mm});
            skPoint(sketch, "E14.14.56.0", {"position": v(433.14, 6.28) * mm});
            skLineSegment(sketch, "E14.15.56.0", {"start": v(427.7, 5.58) * mm, "end": v(428.36, 6.5) * mm});
            skArc(sketch, "E14.18.56.0", {"start": v(433.36, 5.58) * mm, "mid": v(433.8, 5.21) * mm, "end": v(434.34, 5.08) * mm});
            skPoint(sketch, "E14.22.56.0", {"position": v(427.92, 6.28) * mm});
            skLineSegment(sketch, "E14.0.57.0", {"start": v(434.34, 0) * mm, "end": v(441.96, 0) * mm});
            skArc(sketch, "E14.3.57.0", {"start": v(440.32, 6.5) * mm, "mid": v(438.15, 7.62) * mm, "end": v(435.98, 6.5) * mm});
            skLineSegment(sketch, "E14.7.57.0", {"start": v(440.32, 6.5) * mm, "end": v(440.98, 5.58) * mm});
            skArc(sketch, "E14.10.57.0", {"start": v(434.34, 5.08) * mm, "mid": v(434.89, 5.21) * mm, "end": v(435.32, 5.58) * mm});
            skPoint(sketch, "E14.14.57.0", {"position": v(440.76, 6.28) * mm});
            skLineSegment(sketch, "E14.15.57.0", {"start": v(435.32, 5.58) * mm, "end": v(435.98, 6.5) * mm});
            skArc(sketch, "E14.18.57.0", {"start": v(440.98, 5.58) * mm, "mid": v(441.41, 5.21) * mm, "end": v(441.96, 5.08) * mm});
            skPoint(sketch, "E14.22.57.0", {"position": v(435.54, 6.28) * mm});
            skLineSegment(sketch, "E14.0.58.0", {"start": v(441.96, 0) * mm, "end": v(449.58, 0) * mm});
            skArc(sketch, "E14.3.58.0", {"start": v(447.94, 6.5) * mm, "mid": v(445.77, 7.62) * mm, "end": v(443.6, 6.5) * mm});
            skLineSegment(sketch, "E14.7.58.0", {"start": v(447.94, 6.5) * mm, "end": v(448.6, 5.58) * mm});
            skArc(sketch, "E14.10.58.0", {"start": v(441.96, 5.08) * mm, "mid": v(442.5, 5.21) * mm, "end": v(442.94, 5.58) * mm});
            skPoint(sketch, "E14.14.58.0", {"position": v(448.38, 6.28) * mm});
            skLineSegment(sketch, "E14.15.58.0", {"start": v(442.94, 5.58) * mm, "end": v(443.6, 6.5) * mm});
            skArc(sketch, "E14.18.58.0", {"start": v(448.6, 5.58) * mm, "mid": v(449.03, 5.21) * mm, "end": v(449.58, 5.08) * mm});
            skPoint(sketch, "E14.22.58.0", {"position": v(443.16, 6.28) * mm});
            skLineSegment(sketch, "E14.0.59.0", {"start": v(449.58, 0) * mm, "end": v(457.2, 0) * mm});
            skArc(sketch, "E14.3.59.0", {"start": v(455.56, 6.5) * mm, "mid": v(453.4, 7.62) * mm, "end": v(451.22, 6.5) * mm});
            skLineSegment(sketch, "E14.7.59.0", {"start": v(455.56, 6.5) * mm, "end": v(456.22, 5.58) * mm});
            skArc(sketch, "E14.10.59.0", {"start": v(449.58, 5.08) * mm, "mid": v(450.13, 5.21) * mm, "end": v(450.56, 5.58) * mm});
            skPoint(sketch, "E14.14.59.0", {"position": v(456, 6.28) * mm});
            skLineSegment(sketch, "E14.15.59.0", {"start": v(450.56, 5.58) * mm, "end": v(451.22, 6.5) * mm});
            skArc(sketch, "E14.18.59.0", {"start": v(456.22, 5.58) * mm, "mid": v(456.65, 5.21) * mm, "end": v(457.2, 5.08) * mm});
            skPoint(sketch, "E14.22.59.0", {"position": v(450.78, 6.28) * mm});
            skLineSegment(sketch, "E14.0.60.0", {"start": v(457.2, 0) * mm, "end": v(464.82, 0) * mm});
            skArc(sketch, "E14.3.60.0", {"start": v(463.18, 6.5) * mm, "mid": v(461.01, 7.62) * mm, "end": v(458.84, 6.5) * mm});
            skLineSegment(sketch, "E14.7.60.0", {"start": v(463.18, 6.5) * mm, "end": v(463.84, 5.58) * mm});
            skArc(sketch, "E14.10.60.0", {"start": v(457.2, 5.08) * mm, "mid": v(457.75, 5.21) * mm, "end": v(458.18, 5.58) * mm});
            skPoint(sketch, "E14.14.60.0", {"position": v(463.62, 6.28) * mm});
            skLineSegment(sketch, "E14.15.60.0", {"start": v(458.18, 5.58) * mm, "end": v(458.84, 6.5) * mm});
            skArc(sketch, "E14.18.60.0", {"start": v(463.84, 5.58) * mm, "mid": v(464.27, 5.21) * mm, "end": v(464.82, 5.08) * mm});
            skPoint(sketch, "E14.22.60.0", {"position": v(458.4, 6.28) * mm});
            skLineSegment(sketch, "E14.0.61.0", {"start": v(464.82, 0) * mm, "end": v(472.44, 0) * mm});
            skArc(sketch, "E14.3.61.0", {"start": v(470.8, 6.5) * mm, "mid": v(468.63, 7.62) * mm, "end": v(466.46, 6.5) * mm});
            skLineSegment(sketch, "E14.7.61.0", {"start": v(470.8, 6.5) * mm, "end": v(471.46, 5.58) * mm});
            skArc(sketch, "E14.10.61.0", {"start": v(464.82, 5.08) * mm, "mid": v(465.37, 5.21) * mm, "end": v(465.8, 5.58) * mm});
            skPoint(sketch, "E14.14.61.0", {"position": v(471.24, 6.28) * mm});
            skLineSegment(sketch, "E14.15.61.0", {"start": v(465.8, 5.58) * mm, "end": v(466.46, 6.5) * mm});
            skArc(sketch, "E14.18.61.0", {"start": v(471.46, 5.58) * mm, "mid": v(471.9, 5.21) * mm, "end": v(472.44, 5.08) * mm});
            skPoint(sketch, "E14.22.61.0", {"position": v(466.02, 6.28) * mm});
            skLineSegment(sketch, "E14.0.62.0", {"start": v(472.44, 0) * mm, "end": v(480.06, 0) * mm});
            skArc(sketch, "E14.3.62.0", {"start": v(478.42, 6.5) * mm, "mid": v(476.25, 7.62) * mm, "end": v(474.08, 6.5) * mm});
            skLineSegment(sketch, "E14.7.62.0", {"start": v(478.42, 6.5) * mm, "end": v(479.08, 5.58) * mm});
            skArc(sketch, "E14.10.62.0", {"start": v(472.44, 5.08) * mm, "mid": v(472.99, 5.21) * mm, "end": v(473.42, 5.58) * mm});
            skPoint(sketch, "E14.14.62.0", {"position": v(478.86, 6.28) * mm});
            skLineSegment(sketch, "E14.15.62.0", {"start": v(473.42, 5.58) * mm, "end": v(474.08, 6.5) * mm});
            skArc(sketch, "E14.18.62.0", {"start": v(479.08, 5.58) * mm, "mid": v(479.51, 5.21) * mm, "end": v(480.06, 5.08) * mm});
            skPoint(sketch, "E14.22.62.0", {"position": v(473.64, 6.28) * mm});
            skLineSegment(sketch, "E14.0.63.0", {"start": v(480.06, 0) * mm, "end": v(487.68, 0) * mm});
            skArc(sketch, "E14.3.63.0", {"start": v(486.04, 6.5) * mm, "mid": v(483.87, 7.62) * mm, "end": v(481.7, 6.5) * mm});
            skLineSegment(sketch, "E14.7.63.0", {"start": v(486.04, 6.5) * mm, "end": v(486.7, 5.58) * mm});
            skArc(sketch, "E14.10.63.0", {"start": v(480.06, 5.08) * mm, "mid": v(480.6, 5.21) * mm, "end": v(481.04, 5.58) * mm});
            skPoint(sketch, "E14.14.63.0", {"position": v(486.48, 6.28) * mm});
            skLineSegment(sketch, "E14.15.63.0", {"start": v(481.04, 5.58) * mm, "end": v(481.7, 6.5) * mm});
            skArc(sketch, "E14.18.63.0", {"start": v(486.7, 5.58) * mm, "mid": v(487.13, 5.21) * mm, "end": v(487.68, 5.08) * mm});
            skPoint(sketch, "E14.22.63.0", {"position": v(481.26, 6.28) * mm});
            skLineSegment(sketch, "E14.0.64.0", {"start": v(487.68, 0) * mm, "end": v(495.3, 0) * mm});
            skArc(sketch, "E14.3.64.0", {"start": v(493.66, 6.5) * mm, "mid": v(491.5, 7.62) * mm, "end": v(489.32, 6.5) * mm});
            skLineSegment(sketch, "E14.7.64.0", {"start": v(493.66, 6.5) * mm, "end": v(494.32, 5.58) * mm});
            skArc(sketch, "E14.10.64.0", {"start": v(487.68, 5.08) * mm, "mid": v(488.23, 5.21) * mm, "end": v(488.66, 5.58) * mm});
            skPoint(sketch, "E14.14.64.0", {"position": v(494.1, 6.28) * mm});
            skLineSegment(sketch, "E14.15.64.0", {"start": v(488.66, 5.58) * mm, "end": v(489.32, 6.5) * mm});
            skArc(sketch, "E14.18.64.0", {"start": v(494.32, 5.58) * mm, "mid": v(494.75, 5.21) * mm, "end": v(495.3, 5.08) * mm});
            skPoint(sketch, "E14.22.64.0", {"position": v(488.88, 6.28) * mm});
            skLineSegment(sketch, "E14.0.65.0", {"start": v(495.3, 0) * mm, "end": v(502.92, 0) * mm});
            skArc(sketch, "E14.3.65.0", {"start": v(501.28, 6.5) * mm, "mid": v(499.1, 7.62) * mm, "end": v(496.94, 6.5) * mm});
            skLineSegment(sketch, "E14.7.65.0", {"start": v(501.28, 6.5) * mm, "end": v(501.94, 5.58) * mm});
            skArc(sketch, "E14.10.65.0", {"start": v(495.3, 5.08) * mm, "mid": v(495.85, 5.21) * mm, "end": v(496.28, 5.58) * mm});
            skPoint(sketch, "E14.14.65.0", {"position": v(501.72, 6.28) * mm});
            skLineSegment(sketch, "E14.15.65.0", {"start": v(496.28, 5.58) * mm, "end": v(496.94, 6.5) * mm});
            skArc(sketch, "E14.18.65.0", {"start": v(501.94, 5.58) * mm, "mid": v(502.37, 5.21) * mm, "end": v(502.92, 5.08) * mm});
            skPoint(sketch, "E14.22.65.0", {"position": v(496.5, 6.28) * mm});
            skLineSegment(sketch, "E14.0.66.0", {"start": v(502.92, 0) * mm, "end": v(510.54, 0) * mm});
            skArc(sketch, "E14.3.66.0", {"start": v(508.9, 6.5) * mm, "mid": v(506.73, 7.62) * mm, "end": v(504.56, 6.5) * mm});
            skLineSegment(sketch, "E14.7.66.0", {"start": v(508.9, 6.5) * mm, "end": v(509.56, 5.58) * mm});
            skArc(sketch, "E14.10.66.0", {"start": v(502.92, 5.08) * mm, "mid": v(503.47, 5.21) * mm, "end": v(503.9, 5.58) * mm});
            skPoint(sketch, "E14.14.66.0", {"position": v(509.34, 6.28) * mm});
            skLineSegment(sketch, "E14.15.66.0", {"start": v(503.9, 5.58) * mm, "end": v(504.56, 6.5) * mm});
            skArc(sketch, "E14.18.66.0", {"start": v(509.56, 5.58) * mm, "mid": v(510, 5.21) * mm, "end": v(510.54, 5.08) * mm});
            skPoint(sketch, "E14.22.66.0", {"position": v(504.12, 6.28) * mm});
            skLineSegment(sketch, "E14.0.67.0", {"start": v(510.54, 0) * mm, "end": v(518.16, 0) * mm});
            skArc(sketch, "E14.3.67.0", {"start": v(516.52, 6.5) * mm, "mid": v(514.35, 7.62) * mm, "end": v(512.18, 6.5) * mm});
            skLineSegment(sketch, "E14.7.67.0", {"start": v(516.52, 6.5) * mm, "end": v(517.18, 5.58) * mm});
            skArc(sketch, "E14.10.67.0", {"start": v(510.54, 5.08) * mm, "mid": v(511.09, 5.21) * mm, "end": v(511.52, 5.58) * mm});
            skPoint(sketch, "E14.14.67.0", {"position": v(516.96, 6.28) * mm});
            skLineSegment(sketch, "E14.15.67.0", {"start": v(511.52, 5.58) * mm, "end": v(512.18, 6.5) * mm});
            skArc(sketch, "E14.18.67.0", {"start": v(517.18, 5.58) * mm, "mid": v(517.61, 5.21) * mm, "end": v(518.16, 5.08) * mm});
            skPoint(sketch, "E14.22.67.0", {"position": v(511.74, 6.28) * mm});
            skLineSegment(sketch, "E14.0.68.0", {"start": v(518.16, 0) * mm, "end": v(525.78, 0) * mm});
            skArc(sketch, "E14.3.68.0", {"start": v(524.14, 6.5) * mm, "mid": v(521.97, 7.62) * mm, "end": v(519.8, 6.5) * mm});
            skLineSegment(sketch, "E14.7.68.0", {"start": v(524.14, 6.5) * mm, "end": v(524.8, 5.58) * mm});
            skArc(sketch, "E14.10.68.0", {"start": v(518.16, 5.08) * mm, "mid": v(518.7, 5.21) * mm, "end": v(519.14, 5.58) * mm});
            skPoint(sketch, "E14.14.68.0", {"position": v(524.58, 6.28) * mm});
            skLineSegment(sketch, "E14.15.68.0", {"start": v(519.14, 5.58) * mm, "end": v(519.8, 6.5) * mm});
            skArc(sketch, "E14.18.68.0", {"start": v(524.8, 5.58) * mm, "mid": v(525.23, 5.21) * mm, "end": v(525.78, 5.08) * mm});
            skPoint(sketch, "E14.22.68.0", {"position": v(519.36, 6.28) * mm});
            skLineSegment(sketch, "E14.0.69.0", {"start": v(525.78, 0) * mm, "end": v(533.4, 0) * mm});
            skArc(sketch, "E14.3.69.0", {"start": v(531.76, 6.5) * mm, "mid": v(529.6, 7.62) * mm, "end": v(527.42, 6.5) * mm});
            skLineSegment(sketch, "E14.7.69.0", {"start": v(531.76, 6.5) * mm, "end": v(532.42, 5.58) * mm});
            skArc(sketch, "E14.10.69.0", {"start": v(525.78, 5.08) * mm, "mid": v(526.33, 5.21) * mm, "end": v(526.76, 5.58) * mm});
            skPoint(sketch, "E14.14.69.0", {"position": v(532.2, 6.28) * mm});
            skLineSegment(sketch, "E14.15.69.0", {"start": v(526.76, 5.58) * mm, "end": v(527.42, 6.5) * mm});
            skArc(sketch, "E14.18.69.0", {"start": v(532.42, 5.58) * mm, "mid": v(532.85, 5.21) * mm, "end": v(533.4, 5.08) * mm});
            skPoint(sketch, "E14.22.69.0", {"position": v(526.98, 6.28) * mm});
            skLineSegment(sketch, "E14.0.70.0", {"start": v(533.4, 0) * mm, "end": v(541.02, 0) * mm});
            skArc(sketch, "E14.3.70.0", {"start": v(539.38, 6.5) * mm, "mid": v(537.2, 7.62) * mm, "end": v(535.04, 6.5) * mm});
            skLineSegment(sketch, "E14.7.70.0", {"start": v(539.38, 6.5) * mm, "end": v(540.04, 5.58) * mm});
            skArc(sketch, "E14.10.70.0", {"start": v(533.4, 5.08) * mm, "mid": v(533.95, 5.21) * mm, "end": v(534.38, 5.58) * mm});
            skPoint(sketch, "E14.14.70.0", {"position": v(539.82, 6.28) * mm});
            skLineSegment(sketch, "E14.15.70.0", {"start": v(534.38, 5.58) * mm, "end": v(535.04, 6.5) * mm});
            skArc(sketch, "E14.18.70.0", {"start": v(540.04, 5.58) * mm, "mid": v(540.47, 5.21) * mm, "end": v(541.02, 5.08) * mm});
            skPoint(sketch, "E14.22.70.0", {"position": v(534.6, 6.28) * mm});
            skLineSegment(sketch, "E14.0.71.0", {"start": v(541.02, 0) * mm, "end": v(548.64, 0) * mm});
            skArc(sketch, "E14.3.71.0", {"start": v(547, 6.5) * mm, "mid": v(544.83, 7.62) * mm, "end": v(542.66, 6.5) * mm});
            skLineSegment(sketch, "E14.7.71.0", {"start": v(547, 6.5) * mm, "end": v(547.66, 5.58) * mm});
            skArc(sketch, "E14.10.71.0", {"start": v(541.02, 5.08) * mm, "mid": v(541.57, 5.21) * mm, "end": v(542, 5.58) * mm});
            skPoint(sketch, "E14.14.71.0", {"position": v(547.44, 6.28) * mm});
            skLineSegment(sketch, "E14.15.71.0", {"start": v(542, 5.58) * mm, "end": v(542.66, 6.5) * mm});
            skArc(sketch, "E14.18.71.0", {"start": v(547.66, 5.58) * mm, "mid": v(548.1, 5.21) * mm, "end": v(548.64, 5.08) * mm});
            skPoint(sketch, "E14.22.71.0", {"position": v(542.22, 6.28) * mm});
            skLineSegment(sketch, "E14.0.72.0", {"start": v(548.64, 0) * mm, "end": v(556.26, 0) * mm});
            skArc(sketch, "E14.3.72.0", {"start": v(554.62, 6.5) * mm, "mid": v(552.45, 7.62) * mm, "end": v(550.28, 6.5) * mm});
            skLineSegment(sketch, "E14.7.72.0", {"start": v(554.62, 6.5) * mm, "end": v(555.28, 5.58) * mm});
            skArc(sketch, "E14.10.72.0", {"start": v(548.64, 5.08) * mm, "mid": v(549.19, 5.21) * mm, "end": v(549.62, 5.58) * mm});
            skPoint(sketch, "E14.14.72.0", {"position": v(555.06, 6.28) * mm});
            skLineSegment(sketch, "E14.15.72.0", {"start": v(549.62, 5.58) * mm, "end": v(550.28, 6.5) * mm});
            skArc(sketch, "E14.18.72.0", {"start": v(555.28, 5.58) * mm, "mid": v(555.71, 5.21) * mm, "end": v(556.26, 5.08) * mm});
            skPoint(sketch, "E14.22.72.0", {"position": v(549.84, 6.28) * mm});
            skLineSegment(sketch, "E14.0.73.0", {"start": v(556.26, 0) * mm, "end": v(563.88, 0) * mm});
            skArc(sketch, "E14.3.73.0", {"start": v(562.24, 6.5) * mm, "mid": v(560.07, 7.62) * mm, "end": v(557.9, 6.5) * mm});
            skLineSegment(sketch, "E14.7.73.0", {"start": v(562.24, 6.5) * mm, "end": v(562.9, 5.58) * mm});
            skArc(sketch, "E14.10.73.0", {"start": v(556.26, 5.08) * mm, "mid": v(556.8, 5.21) * mm, "end": v(557.24, 5.58) * mm});
            skPoint(sketch, "E14.14.73.0", {"position": v(562.68, 6.28) * mm});
            skLineSegment(sketch, "E14.15.73.0", {"start": v(557.24, 5.58) * mm, "end": v(557.9, 6.5) * mm});
            skArc(sketch, "E14.18.73.0", {"start": v(562.9, 5.58) * mm, "mid": v(563.33, 5.21) * mm, "end": v(563.88, 5.08) * mm});
            skPoint(sketch, "E14.22.73.0", {"position": v(557.46, 6.28) * mm});
            skLineSegment(sketch, "E14.0.74.0", {"start": v(563.88, 0) * mm, "end": v(571.5, 0) * mm});
            skArc(sketch, "E14.3.74.0", {"start": v(569.86, 6.5) * mm, "mid": v(567.7, 7.62) * mm, "end": v(565.52, 6.5) * mm});
            skLineSegment(sketch, "E14.7.74.0", {"start": v(569.86, 6.5) * mm, "end": v(570.52, 5.58) * mm});
            skArc(sketch, "E14.10.74.0", {"start": v(563.88, 5.08) * mm, "mid": v(564.43, 5.21) * mm, "end": v(564.86, 5.58) * mm});
            skPoint(sketch, "E14.14.74.0", {"position": v(570.3, 6.28) * mm});
            skLineSegment(sketch, "E14.15.74.0", {"start": v(564.86, 5.58) * mm, "end": v(565.52, 6.5) * mm});
            skArc(sketch, "E14.18.74.0", {"start": v(570.52, 5.58) * mm, "mid": v(570.95, 5.21) * mm, "end": v(571.5, 5.08) * mm});
            skPoint(sketch, "E14.22.74.0", {"position": v(565.08, 6.28) * mm});
            skLineSegment(sketch, "E14.0.75.0", {"start": v(571.5, 0) * mm, "end": v(579.12, 0) * mm});
            skArc(sketch, "E14.3.75.0", {"start": v(577.48, 6.5) * mm, "mid": v(575.31, 7.62) * mm, "end": v(573.14, 6.5) * mm});
            skLineSegment(sketch, "E14.7.75.0", {"start": v(577.48, 6.5) * mm, "end": v(578.14, 5.58) * mm});
            skArc(sketch, "E14.10.75.0", {"start": v(571.5, 5.08) * mm, "mid": v(572.05, 5.21) * mm, "end": v(572.48, 5.58) * mm});
            skPoint(sketch, "E14.14.75.0", {"position": v(577.92, 6.28) * mm});
            skLineSegment(sketch, "E14.15.75.0", {"start": v(572.48, 5.58) * mm, "end": v(573.14, 6.5) * mm});
            skArc(sketch, "E14.18.75.0", {"start": v(578.14, 5.58) * mm, "mid": v(578.57, 5.21) * mm, "end": v(579.12, 5.08) * mm});
            skPoint(sketch, "E14.22.75.0", {"position": v(572.7, 6.28) * mm});
            skLineSegment(sketch, "E14.0.76.0", {"start": v(579.12, 0) * mm, "end": v(586.74, 0) * mm});
            skArc(sketch, "E14.3.76.0", {"start": v(585.1, 6.5) * mm, "mid": v(582.93, 7.62) * mm, "end": v(580.76, 6.5) * mm});
            skLineSegment(sketch, "E14.7.76.0", {"start": v(585.1, 6.5) * mm, "end": v(585.76, 5.58) * mm});
            skArc(sketch, "E14.10.76.0", {"start": v(579.12, 5.08) * mm, "mid": v(579.67, 5.21) * mm, "end": v(580.1, 5.58) * mm});
            skPoint(sketch, "E14.14.76.0", {"position": v(585.54, 6.28) * mm});
            skLineSegment(sketch, "E14.15.76.0", {"start": v(580.1, 5.58) * mm, "end": v(580.76, 6.5) * mm});
            skArc(sketch, "E14.18.76.0", {"start": v(585.76, 5.58) * mm, "mid": v(586.2, 5.21) * mm, "end": v(586.74, 5.08) * mm});
            skPoint(sketch, "E14.22.76.0", {"position": v(580.32, 6.28) * mm});
            skLineSegment(sketch, "E14.0.77.0", {"start": v(586.74, 0) * mm, "end": v(594.36, 0) * mm});
            skArc(sketch, "E14.3.77.0", {"start": v(592.72, 6.5) * mm, "mid": v(590.55, 7.62) * mm, "end": v(588.38, 6.5) * mm});
            skLineSegment(sketch, "E14.7.77.0", {"start": v(592.72, 6.5) * mm, "end": v(593.38, 5.58) * mm});
            skArc(sketch, "E14.10.77.0", {"start": v(586.74, 5.08) * mm, "mid": v(587.29, 5.21) * mm, "end": v(587.72, 5.58) * mm});
            skPoint(sketch, "E14.14.77.0", {"position": v(593.16, 6.28) * mm});
            skLineSegment(sketch, "E14.15.77.0", {"start": v(587.72, 5.58) * mm, "end": v(588.38, 6.5) * mm});
            skArc(sketch, "E14.18.77.0", {"start": v(593.38, 5.58) * mm, "mid": v(593.81, 5.21) * mm, "end": v(594.36, 5.08) * mm});
            skPoint(sketch, "E14.22.77.0", {"position": v(587.94, 6.28) * mm});
            skLineSegment(sketch, "E14.0.78.0", {"start": v(594.36, 0) * mm, "end": v(601.98, 0) * mm});
            skArc(sketch, "E14.3.78.0", {"start": v(600.34, 6.5) * mm, "mid": v(598.17, 7.62) * mm, "end": v(596, 6.5) * mm});
            skLineSegment(sketch, "E14.7.78.0", {"start": v(600.34, 6.5) * mm, "end": v(601, 5.58) * mm});
            skArc(sketch, "E14.10.78.0", {"start": v(594.36, 5.08) * mm, "mid": v(594.9, 5.21) * mm, "end": v(595.34, 5.58) * mm});
            skPoint(sketch, "E14.14.78.0", {"position": v(600.78, 6.28) * mm});
            skLineSegment(sketch, "E14.15.78.0", {"start": v(595.34, 5.58) * mm, "end": v(596, 6.5) * mm});
            skArc(sketch, "E14.18.78.0", {"start": v(601, 5.58) * mm, "mid": v(601.43, 5.21) * mm, "end": v(601.98, 5.08) * mm});
            skPoint(sketch, "E14.22.78.0", {"position": v(595.56, 6.28) * mm});
            skLineSegment(sketch, "E14.0.79.0", {"start": v(601.98, 0) * mm, "end": v(609.6, 0) * mm});
            skArc(sketch, "E14.3.79.0", {"start": v(607.96, 6.5) * mm, "mid": v(605.8, 7.62) * mm, "end": v(603.62, 6.5) * mm});
            skLineSegment(sketch, "E14.7.79.0", {"start": v(607.96, 6.5) * mm, "end": v(608.62, 5.58) * mm});
            skArc(sketch, "E14.10.79.0", {"start": v(601.98, 5.08) * mm, "mid": v(602.53, 5.21) * mm, "end": v(602.96, 5.58) * mm});
            skPoint(sketch, "E14.14.79.0", {"position": v(608.4, 6.28) * mm});
            skLineSegment(sketch, "E14.15.79.0", {"start": v(602.96, 5.58) * mm, "end": v(603.62, 6.5) * mm});
            skArc(sketch, "E14.18.79.0", {"start": v(608.62, 5.58) * mm, "mid": v(609.05, 5.21) * mm, "end": v(609.6, 5.08) * mm});
            skPoint(sketch, "E14.22.79.0", {"position": v(603.18, 6.28) * mm});
            skLineSegment(sketch, "E14.0.80.0", {"start": v(609.6, 0) * mm, "end": v(617.22, 0) * mm});
            skArc(sketch, "E14.3.80.0", {"start": v(615.58, 6.5) * mm, "mid": v(613.41, 7.62) * mm, "end": v(611.24, 6.5) * mm});
            skLineSegment(sketch, "E14.7.80.0", {"start": v(615.58, 6.5) * mm, "end": v(616.24, 5.58) * mm});
            skArc(sketch, "E14.10.80.0", {"start": v(609.6, 5.08) * mm, "mid": v(610.15, 5.21) * mm, "end": v(610.58, 5.58) * mm});
            skPoint(sketch, "E14.14.80.0", {"position": v(616.02, 6.28) * mm});
            skLineSegment(sketch, "E14.15.80.0", {"start": v(610.58, 5.58) * mm, "end": v(611.24, 6.5) * mm});
            skArc(sketch, "E14.18.80.0", {"start": v(616.24, 5.58) * mm, "mid": v(616.67, 5.21) * mm, "end": v(617.22, 5.08) * mm});
            skPoint(sketch, "E14.22.80.0", {"position": v(610.8, 6.28) * mm});
            skLineSegment(sketch, "E14.0.81.0", {"start": v(617.22, 0) * mm, "end": v(624.84, 0) * mm});
            skArc(sketch, "E14.3.81.0", {"start": v(623.2, 6.5) * mm, "mid": v(621.03, 7.62) * mm, "end": v(618.86, 6.5) * mm});
            skLineSegment(sketch, "E14.7.81.0", {"start": v(623.2, 6.5) * mm, "end": v(623.86, 5.58) * mm});
            skArc(sketch, "E14.10.81.0", {"start": v(617.22, 5.08) * mm, "mid": v(617.77, 5.21) * mm, "end": v(618.2, 5.58) * mm});
            skPoint(sketch, "E14.14.81.0", {"position": v(623.64, 6.28) * mm});
            skLineSegment(sketch, "E14.15.81.0", {"start": v(618.2, 5.58) * mm, "end": v(618.86, 6.5) * mm});
            skArc(sketch, "E14.18.81.0", {"start": v(623.86, 5.58) * mm, "mid": v(624.3, 5.21) * mm, "end": v(624.84, 5.08) * mm});
            skPoint(sketch, "E14.22.81.0", {"position": v(618.42, 6.28) * mm});
            skLineSegment(sketch, "E14.0.82.0", {"start": v(624.84, 0) * mm, "end": v(632.46, 0) * mm});
            skArc(sketch, "E14.3.82.0", {"start": v(630.82, 6.5) * mm, "mid": v(628.65, 7.62) * mm, "end": v(626.48, 6.5) * mm});
            skLineSegment(sketch, "E14.7.82.0", {"start": v(630.82, 6.5) * mm, "end": v(631.48, 5.58) * mm});
            skArc(sketch, "E14.10.82.0", {"start": v(624.84, 5.08) * mm, "mid": v(625.39, 5.21) * mm, "end": v(625.82, 5.58) * mm});
            skPoint(sketch, "E14.14.82.0", {"position": v(631.26, 6.28) * mm});
            skLineSegment(sketch, "E14.15.82.0", {"start": v(625.82, 5.58) * mm, "end": v(626.48, 6.5) * mm});
            skArc(sketch, "E14.18.82.0", {"start": v(631.48, 5.58) * mm, "mid": v(631.91, 5.21) * mm, "end": v(632.46, 5.08) * mm});
            skPoint(sketch, "E14.22.82.0", {"position": v(626.04, 6.28) * mm});
            skLineSegment(sketch, "E14.0.83.0", {"start": v(632.46, 0) * mm, "end": v(640.08, 0) * mm});
            skArc(sketch, "E14.3.83.0", {"start": v(638.44, 6.5) * mm, "mid": v(636.27, 7.62) * mm, "end": v(634.1, 6.5) * mm});
            skLineSegment(sketch, "E14.7.83.0", {"start": v(638.44, 6.5) * mm, "end": v(639.1, 5.58) * mm});
            skArc(sketch, "E14.10.83.0", {"start": v(632.46, 5.08) * mm, "mid": v(633, 5.21) * mm, "end": v(633.44, 5.58) * mm});
            skPoint(sketch, "E14.14.83.0", {"position": v(638.88, 6.28) * mm});
            skLineSegment(sketch, "E14.15.83.0", {"start": v(633.44, 5.58) * mm, "end": v(634.1, 6.5) * mm});
            skArc(sketch, "E14.18.83.0", {"start": v(639.1, 5.58) * mm, "mid": v(639.53, 5.21) * mm, "end": v(640.08, 5.08) * mm});
            skPoint(sketch, "E14.22.83.0", {"position": v(633.66, 6.28) * mm});
            skLineSegment(sketch, "E14.0.84.0", {"start": v(640.08, 0) * mm, "end": v(647.7, 0) * mm});
            skArc(sketch, "E14.3.84.0", {"start": v(646.06, 6.5) * mm, "mid": v(643.9, 7.62) * mm, "end": v(641.72, 6.5) * mm});
            skLineSegment(sketch, "E14.7.84.0", {"start": v(646.06, 6.5) * mm, "end": v(646.72, 5.58) * mm});
            skArc(sketch, "E14.10.84.0", {"start": v(640.08, 5.08) * mm, "mid": v(640.63, 5.21) * mm, "end": v(641.06, 5.58) * mm});
            skPoint(sketch, "E14.14.84.0", {"position": v(646.5, 6.28) * mm});
            skLineSegment(sketch, "E14.15.84.0", {"start": v(641.06, 5.58) * mm, "end": v(641.72, 6.5) * mm});
            skArc(sketch, "E14.18.84.0", {"start": v(646.72, 5.58) * mm, "mid": v(647.15, 5.21) * mm, "end": v(647.7, 5.08) * mm});
            skPoint(sketch, "E14.22.84.0", {"position": v(641.28, 6.28) * mm});
            skLineSegment(sketch, "E15", {"start": v(647.7, 0) * mm, "end": v(647.7, 5.08) * mm});
            skLineSegment(sketch, "E16", {"start": v(0, 0) * mm, "end": v(0, 5.08) * mm});
            skSolve(sketch);
        }
        {
            var Q0;
            Q0 = qSketchRegion(id + "F0", true);
            extrude(context, id + "F1", {"entities" : qUnion([Q0]), "depth" : 12.7 * mm});
        }
    });
